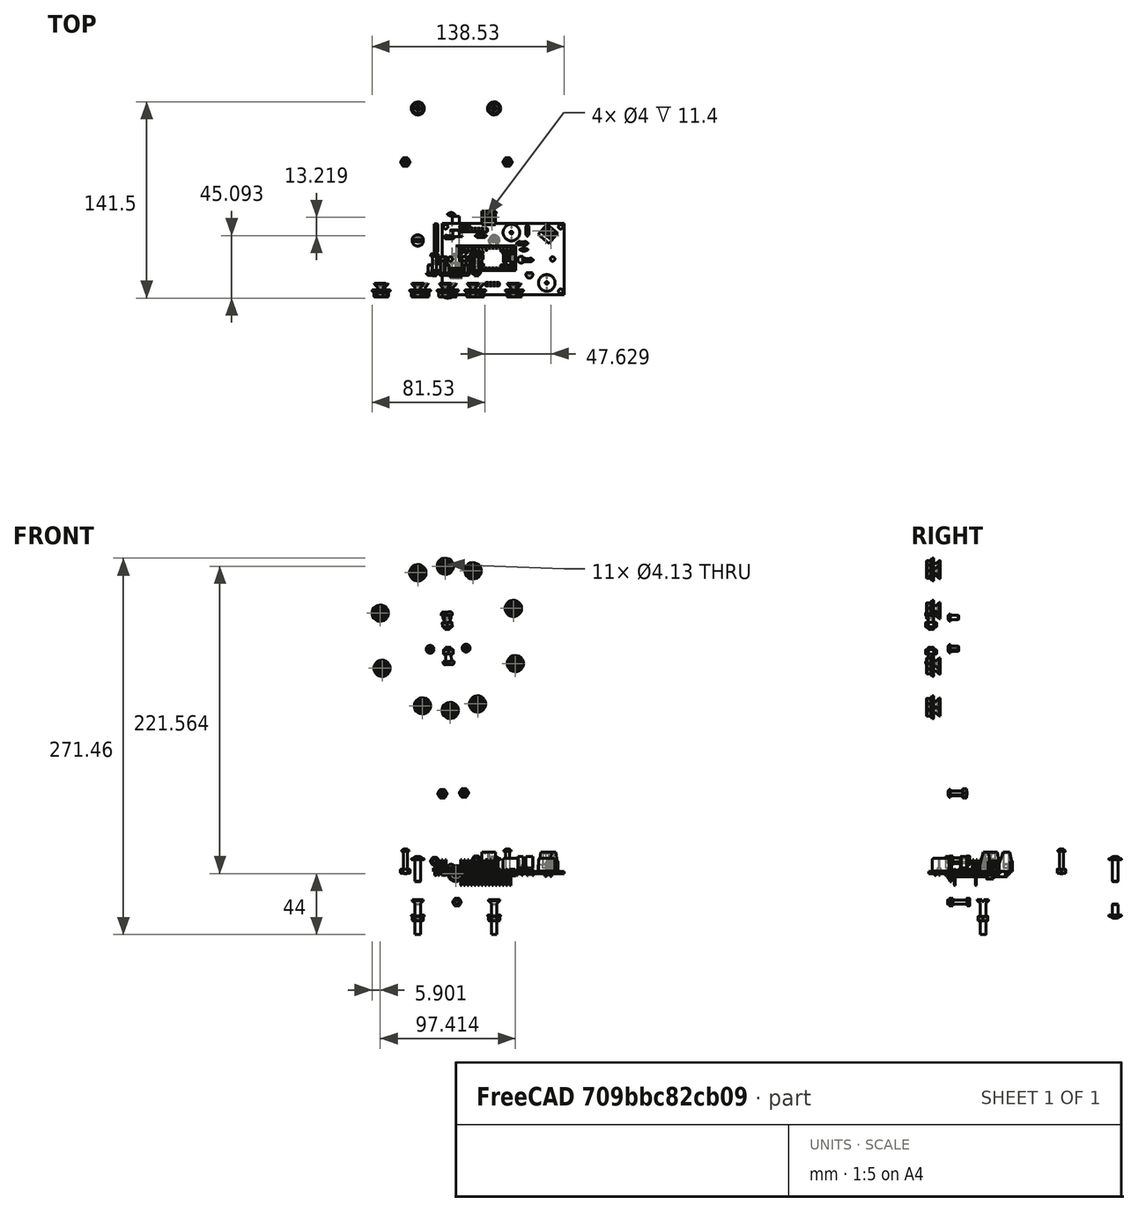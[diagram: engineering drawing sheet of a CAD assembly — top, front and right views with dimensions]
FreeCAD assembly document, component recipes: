
FREECAD ASSEMBLY — COMPONENT RECIPES ("assembly_Pendulum")

This assembly document has 17 components, labeled P0..P16 below (a component is one placed body or linked part). 14 of them carry a construction recipe — the FreeCAD feature program that regenerates the part from scratch, quoted from this document or its linked companion documents; the rest are supplied as boundary geometry only. No exploded tour is included for this assembly.
COMPONENT P0 — recipe-attached ("Body_Support", modeled in this document).
Construction recipe (the document's own serialized feature program — sketch geometry with constraints, then the solid features built on it; lengths are millimeters unless a unit is written):

FEATURE [Sketcher::SketchObject] Sketch
  ArcFitTolerance = 1e-06
  AttachmentSupport = -> [XZ_Plane001]
  ExternalTypes = [0]
  FullyConstrained = true
  MakeInternals = false
  MapMode = 5
  Placement = pos=(0,0,0) rot=(1,0,0;1.5708rad)
  _ExternalGeoVersion = 0
  sketch-geometry (13):
    g0: LineSegment StartX=5.6759 StartY=30.0968 StartZ=0 EndX=23.0689 EndY=6 EndZ=0
    g1: LineSegment StartX=23.0689 StartY=6 StartZ=0 EndX=34 EndY=6 EndZ=0
    g2: LineSegment StartX=34 StartY=6 StartZ=0 EndX=34 EndY=0 EndZ=0
    g3: LineSegment StartX=34 StartY=0 StartZ=0 EndX=20 EndY=0 EndZ=0
    g4: LineSegment StartX=20 StartY=0 StartZ=0 EndX=4.86567 EndY=20.9676 EndZ=0
    g5: LineSegment StartX=-4.86567 StartY=20.9676 StartZ=0 EndX=-20 EndY=0 EndZ=0
    g6: LineSegment StartX=-20 StartY=0 StartZ=0 EndX=-34 EndY=0 EndZ=0
    g7: LineSegment StartX=-34 StartY=0 StartZ=0 EndX=-34 EndY=6 EndZ=0
    g8: LineSegment StartX=-34 StartY=6 StartZ=0 EndX=-23.0689 EndY=6 EndZ=0
    g9: LineSegment StartX=-23.0689 StartY=6 StartZ=0 EndX=-5.6759 EndY=30.0968 EndZ=0
    g10: Circle CenterX=-1e-16 CenterY=26 CenterZ=0 NormalX=0 NormalY=0 NormalZ=1 AngleXU=0 Radius=2.8
    g11: ArcOfCircle CenterX=-1e-16 CenterY=26 CenterZ=0 NormalX=0 NormalY=0 NormalZ=1 AngleXU=0 Radius=7 StartAngle=0.625205 EndAngle=2.51639
    g12: ArcOfCircle CenterX=-1e-16 CenterY=26 CenterZ=0 NormalX=0 NormalY=0 NormalZ=1 AngleXU=0 Radius=7 StartAngle=3.94384 EndAngle=5.48094
  constraints (36):
    c: Coincident(g0,g1)
    c: Horizontal(g1)
    c: Coincident(g1,g2)
    c: PointOnObject(g2,g-1)
    c: Coincident(g2,g3)
    c: PointOnObject(g3,g-1)
    c: Coincident(g3,g4)
    c: Coincident(g5,g6)
    c: PointOnObject(g6,g-1)
    c: Coincident(g6,g7)
    c: Vertical(g7)
    c: Coincident(g7,g8)
    c: Horizontal(g8)
    c: Coincident(g8,g9)
    c: Symmetric(g9,g0,g-2)
    c: Parallel(g9,g5)
    c: Parallel(g0,g4)
    c: Vertical(g2)
    c: Equal(g7,g2)
    c: DistanceY(g7,g7) = 6
    c: Equal(g8,g1)
    c: DistanceX(g6,g6) = 14
    c: DistanceX(g5,g3) = 40
    c: Diameter(g10) = 5.6
    c: Coincident(g11,g10)
    c: Coincident(g11,g0)
    c: Equal(g11,g12)
    c: Coincident(g11,g12)
    c: Coincident(g4,g12)
    c: Coincident(g5,g12)
    c: DistanceY(g-1,g10) = 26
    c: Distance(g5,g9) = 6
    c: Distance(g4,g0) = 6
    c: Tangent(g9,g11) = 1.5708
    c: Diameter(g11) = 14
    c: Symmetric(g5,g3,g-2)
FEATURE [PartDesign::Pad] Pad  label="Pad_Main"
  Direction = (0,-1,2e-16)
  Length = 10
  Length2 = 10
  Placement = pos=(0,0,0) rot=(1,0,0;1.5708rad)
  Profile = -> Sketch
  ReferenceAxis = -> Sketch [N_Axis]
  Refine = true
  SideType = 0
  Suppressed = false
  Type = 0
  Type2 = 0
FEATURE [Sketcher::SketchObject] Sketch001
  ArcFitTolerance = 1e-06
  AttachmentSupport = -> [Pad]
  ExternalGeometry = -> [Pad]
  ExternalTypes = [0]
  FullyConstrained = true
  MakeInternals = false
  MapMode = 5
  Placement = pos=(0,-10,0) rot=(1,0,0;1.5708rad)
  _ExternalGeoVersion = 0
  sketch-geometry (2):
    g0: Circle CenterX=0 CenterY=26 CenterZ=0 NormalX=0 NormalY=0 NormalZ=1 AngleXU=0 Radius=3.8
    g1: Circle CenterX=0 CenterY=26 CenterZ=0 NormalX=0 NormalY=0 NormalZ=1 AngleXU=0 Radius=2.8
  constraints (4):
    c: Coincident(g0,g-3)
    c: Coincident(g1,g0)
    c: Diameter(g1) = 5.6
    c: Diameter(g0) = 7.6
FEATURE [PartDesign::Pad] Pad001  label="Pad_Shaft"
  BaseFeature = -> Pad
  Direction = (0,-1,2e-16)
  Length = 16.6
  Length2 = 10
  Placement = pos=(0,0,0) rot=(1,0,0;1.5708rad)
  Profile = -> Sketch001
  ReferenceAxis = -> Sketch001 [N_Axis]
  Refine = true
  SideType = 0
  Suppressed = false
  Type = 0
  Type2 = 0
FEATURE [Sketcher::SketchObject] Sketch002
  ArcFitTolerance = 1e-06
  AttachmentSupport = -> [Pad001]
  ExternalGeometry = -> [Pad001]
  ExternalTypes = [0]
  FullyConstrained = true
  MakeInternals = false
  MapMode = 5
  Placement = pos=(0,-10,0) rot=(1,0,0;1.5708rad)
  _ExternalGeoVersion = 0
  sketch-geometry (2):
    g0: Circle CenterX=0 CenterY=26 CenterZ=0 NormalX=0 NormalY=0 NormalZ=1 AngleXU=0 Radius=3.8
    g1: Circle CenterX=0 CenterY=26 CenterZ=0 NormalX=0 NormalY=0 NormalZ=1 AngleXU=0 Radius=6.5
  constraints (4):
    c: Coincident(g0,g-3)
    c: Equal(g0,g-3)
    c: Coincident(g1,g0)
    c: Diameter(g1) = 13
FEATURE [PartDesign::Pad] Pad002  label="Pad_Thrust"
  BaseFeature = -> Pad001
  Direction = (0,-1,2e-16)
  Length = 10
  Length2 = 10
  Placement = pos=(0,0,0) rot=(1,0,0;1.5708rad)
  Profile = -> Sketch002
  ReferenceAxis = -> Sketch002 [N_Axis]
  Refine = true
  SideType = 0
  Suppressed = false
  Type = 0
  Type2 = 0
FEATURE [Sketcher::SketchObject] Sketch003
  ArcFitTolerance = 1e-06
  AttachmentSupport = -> [Pad002]
  ExternalTypes = [0]
  FullyConstrained = true
  MakeInternals = false
  MapMode = 5
  Placement = pos=(0,2.9e-15,0) rot=(-1,0,0;1.5708rad)
  _ExternalGeoVersion = 0
  sketch-geometry (7):
    g0: LineSegment StartX=-4.8 StartY=-26 StartZ=0 EndX=-2.4 EndY=-30.1569 EndZ=0
    g1: LineSegment StartX=-2.4 StartY=-30.1569 StartZ=0 EndX=2.4 EndY=-30.1569 EndZ=0
    g2: LineSegment StartX=2.4 StartY=-30.1569 StartZ=0 EndX=4.8 EndY=-26 EndZ=0
    g3: LineSegment StartX=4.8 StartY=-26 StartZ=0 EndX=2.4 EndY=-21.8431 EndZ=0
    g4: LineSegment StartX=2.4 StartY=-21.8431 StartZ=0 EndX=-2.4 EndY=-21.8431 EndZ=0
    g5: LineSegment StartX=-2.4 StartY=-21.8431 StartZ=0 EndX=-4.8 EndY=-26 EndZ=0
    g6: Circle [constr] CenterX=0 CenterY=-26 CenterZ=0 NormalX=0 NormalY=0 NormalZ=1 AngleXU=0 Radius=4.8
  constraints (16):
    c: Coincident(g0,g1)
    c: Coincident(g1,g2)
    c: Coincident(g2,g3)
    c: Coincident(g3,g4)
    c: Coincident(g4,g5)
    c: Coincident(g5,g0)
    c: Equal(g0, g1-g5) x5
    c: PointOnObject(g0,g6)
    c: PointOnObject(g1,g6)
    c: PointOnObject(g2,g6)
    c: PointOnObject(g3,g6)
    c: PointOnObject(g4,g6)
    c: PointOnObject(g5,g6)
    c: Coincident(g6,g-3)
    c: Horizontal(g4)
    c: Diameter(g6) = 9.6
FEATURE [PartDesign::Pocket] Pocket
  BaseFeature = -> Pad002
  Direction = (0,-1,-2e-16)
  Length = 3
  Length2 = 5
  Placement = pos=(0,0,0) rot=(1,0,0;1.5708rad)
  Profile = -> Sketch003
  ReferenceAxis = -> Sketch003 [N_Axis]
  Refine = true
  SideType = 0
  Suppressed = false
  Type = 0
  Type2 = 0
FEATURE [PartDesign::CoordinateSystem] Support
  AttacherType = Attacher::AttachEngine3D
  AttachmentOffset = pos=(0,0,0) rot=(-0.57735,0.57735,-0.57735;2.0944rad)
  AttachmentSupport = -> [Pocket]
  MapMode = 11
  Placement = pos=(0,-26.6,26) rot=(0,0,1;0rad)
FEATURE [Sketcher::SketchObject] Sketch050
  ArcFitTolerance = 1e-06
  AttachmentSupport = -> [XY_Plane001]
  ExternalTypes = [0]
  FullyConstrained = true
  MakeInternals = false
  MapMode = 5
  _ExternalGeoVersion = 0
  sketch-geometry (2):
    g0: Circle CenterX=-27.5 CenterY=-5 CenterZ=0 NormalX=0 NormalY=0 NormalZ=1 AngleXU=0 Radius=2.3
    g1: Circle CenterX=27.5 CenterY=-5 CenterZ=0 NormalX=0 NormalY=0 NormalZ=1 AngleXU=0 Radius=2.3
  constraints (5):
    c: Equal(g1,g0)
    c: Diameter(g1) = 4.6
    c: DistanceX(g0,g1) = 55
    c: DistanceY(g1,g-1) = 5
    c: Symmetric(g1,g0,g-2)
FEATURE [PartDesign::Pocket] Pocket015
  BaseFeature = -> Pocket
  Direction = (0,0,-1)
  Length = 5
  Length2 = 5
  Placement = pos=(0,0,0) rot=(1,0,0;1.5708rad)
  Profile = -> Sketch050
  ReferenceAxis = -> Sketch050 [N_Axis]
  Refine = true
  Reversed = true
  SideType = 0
  Suppressed = false
  Type = 1
  Type2 = 0
FEATURE [PartDesign::Chamfer] Chamfer003
  Angle = 45
  Base = -> Pocket015 [Edge47,Edge40]
  BaseFeature = -> Pocket015
  ChamferType = 0
  FlipDirection = false
  Placement = pos=(0,0,0) rot=(1,0,0;1.5708rad)
  Refine = true
  Size = 1.5
  Size2 = 1
  SupportTransform = false
  Suppressed = false
  UseAllEdges = false
FEATURE [PartDesign::CoordinateSystem] Support_Foot
  AttacherType = Attacher::AttachEngine3D
  AttachmentOffset = pos=(0,0,0) rot=(0.866025,-0.5,0;3.14159rad)
  AttachmentSupport = -> [Pocket015]
  MapMode = 11
  Placement = pos=(-27.5,-5,6) rot=(0,0,1;5.75959rad)
FEATURE [PartDesign::Fillet] Fillet010
  Base = -> Pocket015 [Edge31,Edge16,Edge13,Edge28]
  BaseFeature = -> Pocket015
  Placement = pos=(0,0,0) rot=(1,0,0;1.5708rad)
  Radius = 4.99
  Refine = true
  SupportTransform = false
  Suppressed = false
  UseAllEdges = false
FEATURE [PartDesign::Body] Body  label="Body_Support"
  AllowCompound = false
  Description = Pendulum
  Group = -> [Sketch,Pad,Sketch001,Pad001,Sketch002,Pad002,Sketch003,Pocket,Support,Sketch050,Pocket015,Chamfer003,Support_Foot,Fillet010]
  Origin = -> Origin001
  Tip = -> Fillet010
COMPONENT P1 — recipe-attached ("Body_Bearing", modeled in this document).
Construction recipe (the document's own serialized feature program — sketch geometry with constraints, then the solid features built on it; lengths are millimeters unless a unit is written):

FEATURE [Sketcher::SketchObject] Sketch005  label="Sketch_section"
  ArcFitTolerance = 0
  AttachmentSupport = -> [XZ_Plane003]
  ExternalTypes = [0]
  FullyConstrained = true
  MakeInternals = false
  MapMode = 5
  Placement = pos=(0,0,0) rot=(1,0,0;1.5708rad)
  _ExternalGeoVersion = 0
  sketch-geometry (12):
    g0: LineSegment StartX=4 StartY=-3.5 StartZ=0 EndX=6.5 EndY=-3.5 EndZ=0
    g1: LineSegment StartX=11 StartY=-3.5 StartZ=0 EndX=11 EndY=3.5 EndZ=0
    g2: LineSegment StartX=11 StartY=3.5 StartZ=0 EndX=9.25 EndY=3.5 EndZ=0
    g3: LineSegment StartX=4 StartY=3.5 StartZ=0 EndX=4 EndY=-3.5 EndZ=0
    g4: LineSegment StartX=6.5 StartY=3.5 StartZ=0 EndX=6.75 EndY=3.25 EndZ=0
    g5: LineSegment StartX=6.75 StartY=3.25 StartZ=0 EndX=9 EndY=3.25 EndZ=0
    g6: LineSegment StartX=9 StartY=3.25 StartZ=0 EndX=9.25 EndY=3.5 EndZ=0
    g7: LineSegment StartX=6.5 StartY=-3.5 StartZ=0 EndX=6.75 EndY=-3.25 EndZ=0
    g8: LineSegment StartX=6.75 StartY=-3.25 StartZ=0 EndX=9 EndY=-3.25 EndZ=0
    g9: LineSegment StartX=9 StartY=-3.25 StartZ=0 EndX=9.25 EndY=-3.5 EndZ=0
    g10: LineSegment StartX=6.5 StartY=3.5 StartZ=0 EndX=4 EndY=3.5 EndZ=0
    g11: LineSegment StartX=9.25 StartY=-3.5 StartZ=0 EndX=11 EndY=-3.5 EndZ=0
  constraints (33):
    c: Coincident(g11,g1)
    c: Coincident(g1,g2)
    c: Coincident(g10,g3)
    c: Coincident(g3,g0)
    c: Horizontal(g0)
    c: Horizontal(g2)
    c: Vertical(g1)
    c: DistanceY(g1) = 7
    c: DistanceX(g0) = 4
    c: DistanceX(g11) = 11
    c: Coincident(g4,g5)
    c: Horizontal(g5)
    c: Coincident(g5,g6)
    c: Coincident(g7,g8)
    c: Horizontal(g8)
    c: Coincident(g8,g9)
    c: Coincident(g2,g6)
    c: Coincident(g10,g4)
    c: Tangent(g2,g10)
    c: Coincident(g0,g7)
    c: Coincident(g11,g9)
    c: Tangent(g0,g11)
    c: Equal(g4,g6)
    c: Equal(g6,g7)
    c: Angle(g10,g4) = 2.35619
    c: DistanceX(g2) = -1.75
    c: DistanceX(g10) = -2.5
    c: Equal(g0,g10)
    c: Equal(g11,g2)
    c: Equal(g9,g7)
    c: Parallel(g9,g4)
    c: DistanceY(g5,g1) = 0.25
    c: Symmetric(g0,g3,g-1)
FEATURE [PartDesign::Revolution] Revolution
  Angle = 360
  Angle2 = 60
  Axis = (0,2e-16,1)
  Base = (0,0,0)
  FuseOrder = 1
  Placement = pos=(0,0,0) rot=(1,0,0;1.5708rad)
  Profile = -> Sketch005
  ReferenceAxis = -> Sketch005 [V_Axis]
  Refine = true
  Suppressed = false
  Type = 0
FEATURE [PartDesign::Chamfer] Chamfer
  Angle = 45
  Base = -> Revolution [Edge12,Edge11]
  BaseFeature = -> Revolution
  ChamferType = 0
  FlipDirection = false
  Placement = pos=(0,0,0) rot=(1,0,0;1.5708rad)
  Refine = true
  Size = 0.25
  Size2 = 1
  SupportTransform = false
  Suppressed = false
  UseAllEdges = false
FEATURE [PartDesign::CoordinateSystem] Bearing_Axis
  AttacherType = Attacher::AttachEngine3D
  AttachmentSupport = -> [Chamfer]
  MapMode = 45
  Placement = pos=(1.89e-14,1.7e-15,3.5) rot=(0,0,1;0rad)
FEATURE [PartDesign::Body] Body002  label="Body_Bearing"
  AllowCompound = false
  Group = -> [Sketch005,Revolution,Chamfer,Bearing_Axis]
  Origin = -> Origin003
  Tip = -> Chamfer
COMPONENT P2 — recipe-attached ("Body_Arm", modeled in this document).
Construction recipe (the document's own serialized feature program — sketch geometry with constraints, then the solid features built on it; lengths are millimeters unless a unit is written):

FEATURE [Sketcher::SketchObject] Sketch006
  ArcFitTolerance = 1e-06
  AttachmentSupport = -> [XY_Plane004]
  ExternalTypes = [0]
  FullyConstrained = true
  MakeInternals = false
  MapMode = 5
  _ExternalGeoVersion = 0
  sketch-geometry (1):
    g0: Circle CenterX=0 CenterY=84.85 CenterZ=0 NormalX=0 NormalY=0 NormalZ=1 AngleXU=0 Radius=23
  constraints (3):
    c: PointOnObject(g0,g-2)
    c: DistanceY(g-1,g0) = 84.85
    c: Diameter(g0) = 46
FEATURE [Sketcher::SketchObject] Sketch007
  ArcFitTolerance = 1e-06
  AttachmentSupport = -> [XY_Plane004]
  ExternalTypes = [0]
  FullyConstrained = true
  MakeInternals = false
  MapMode = 5
  _ExternalGeoVersion = 0
  sketch-geometry (33):
    g0: LineSegment StartX=-18 StartY=67.5 StartZ=0 EndX=-18 EndY=-67.5 EndZ=0
    g1: LineSegment StartX=18 StartY=-67.5 StartZ=0 EndX=18 EndY=67.5 EndZ=0
    g2: ArcOfCircle CenterX=0 CenterY=84.8494 CenterZ=0 NormalX=0 NormalY=0 NormalZ=1 AngleXU=0 Radius=25 StartAngle=5.51619 EndAngle=10.1918
    g3: Circle CenterX=0 CenterY=84.8494 CenterZ=0 NormalX=0 NormalY=0 NormalZ=1 AngleXU=0 Radius=11.5
    g4: Circle CenterX=0 CenterY=99.8494 CenterZ=0 NormalX=0 NormalY=0 NormalZ=1 AngleXU=0 Radius=1.8
    g5: Circle CenterX=9.64181 CenterY=96.34 CenterZ=0 NormalX=0 NormalY=0 NormalZ=1 AngleXU=0 Radius=1.8
    g6: Circle CenterX=14.7721 CenterY=87.4541 CenterZ=0 NormalX=0 NormalY=0 NormalZ=1 AngleXU=0 Radius=1.8
    g7: Circle CenterX=12.9904 CenterY=77.3494 CenterZ=0 NormalX=0 NormalY=0 NormalZ=1 AngleXU=0 Radius=1.8
    g8: Circle CenterX=5.1303 CenterY=70.754 CenterZ=0 NormalX=0 NormalY=0 NormalZ=1 AngleXU=0 Radius=1.8
    g9: Circle CenterX=-5.1303 CenterY=70.754 CenterZ=0 NormalX=0 NormalY=0 NormalZ=1 AngleXU=0 Radius=1.8
    g10: Circle CenterX=-12.9904 CenterY=77.3494 CenterZ=0 NormalX=0 NormalY=0 NormalZ=1 AngleXU=0 Radius=1.8
    g11: Circle CenterX=-14.7721 CenterY=87.4541 CenterZ=0 NormalX=0 NormalY=0 NormalZ=1 AngleXU=0 Radius=1.8
    g12: Circle CenterX=-9.64181 CenterY=96.34 CenterZ=0 NormalX=0 NormalY=0 NormalZ=1 AngleXU=0 Radius=1.8
    g13: LineSegment [constr] StartX=-9.64181 StartY=96.34 StartZ=0 EndX=0 EndY=84.8494 EndZ=0
    g14: LineSegment [constr] StartX=-14.7721 StartY=87.4541 StartZ=0 EndX=0 EndY=84.8494 EndZ=0
    g15: LineSegment [constr] StartX=-12.9904 StartY=77.3494 StartZ=0 EndX=0 EndY=84.8494 EndZ=0
    g16: LineSegment [constr] StartX=-5.1303 StartY=70.754 StartZ=0 EndX=0 EndY=84.8494 EndZ=0
    g17: LineSegment [constr] StartX=5.1303 StartY=70.754 StartZ=0 EndX=0 EndY=84.8494 EndZ=0
    g18: LineSegment [constr] StartX=12.9904 StartY=77.3494 StartZ=0 EndX=0 EndY=84.8494 EndZ=0
    g19: LineSegment [constr] StartX=14.7721 StartY=87.4541 StartZ=0 EndX=0 EndY=84.8494 EndZ=0
    g20: LineSegment [constr] StartX=9.64181 StartY=96.34 StartZ=0 EndX=0 EndY=84.8494 EndZ=0
    g21: Circle CenterX=-7.78 CenterY=-27 CenterZ=0 NormalX=0 NormalY=0 NormalZ=1 AngleXU=0 Radius=1.8
    g22: Circle CenterX=7.78 CenterY=-27 CenterZ=0 NormalX=0 NormalY=0 NormalZ=1 AngleXU=0 Radius=1.8
    g23: ArcOfCircle CenterX=0 CenterY=-84.8494 CenterZ=0 NormalX=0 NormalY=0 NormalZ=1 AngleXU=0 Radius=25 StartAngle=2.3746 EndAngle=7.05018
    g24: Circle CenterX=0 CenterY=-84.8494 CenterZ=0 NormalX=0 NormalY=0 NormalZ=1 AngleXU=0 Radius=11.25
    g25: LineSegment StartX=-12.5 StartY=63.1987 StartZ=0 EndX=-12.5 EndY=-16.8013 EndZ=0
    g26: LineSegment StartX=-12.5 StartY=-16.8013 StartZ=0 EndX=12.5 EndY=-16.8013 EndZ=0
    g27: LineSegment StartX=12.5 StartY=-16.8013 StartZ=0 EndX=12.5 EndY=63.1987 EndZ=0
    g28: LineSegment StartX=-12.5 StartY=-33.5 StartZ=0 EndX=-12.5 EndY=-67.5 EndZ=0
    g29: LineSegment StartX=-12.5 StartY=-67.5 StartZ=0 EndX=12.5 EndY=-67.5 EndZ=0
    g30: LineSegment StartX=12.5 StartY=-67.5 StartZ=0 EndX=12.5 EndY=-33.5 EndZ=0
    g31: LineSegment StartX=12.5 StartY=-33.5 StartZ=0 EndX=-12.5 EndY=-33.5 EndZ=0
    g32: ArcOfCircle CenterX=0 CenterY=84.8494 CenterZ=0 NormalX=0 NormalY=0 NormalZ=1 AngleXU=0 Radius=25 StartAngle=4.18879 EndAngle=5.23599
  constraints (88):
    c: Vertical(g0)
    c: Vertical(g1)
    c: Symmetric(g0,g1,g-1)
    c: DistanceX(g0,g1) = 36
    c: DistanceY(g1,g1) = 135
    c: PointOnObject(g2,g-2)
    c: Diameter(g2) = 50
    c: Coincident(g2,g0)
    c: Coincident(g2,g1)
    c: Coincident(g3,g2)
    c: Diameter(g3) = 23
    c: PointOnObject(g4,g-2)
    c: Coincident(g13,g12)
    c: Coincident(g13,g2)
    c: Coincident(g14,g11)
    c: Coincident(g14,g2)
    c: Coincident(g15,g10)
    c: Coincident(g15,g2)
    c: Coincident(g16,g9)
    c: Coincident(g16,g2)
    c: Coincident(g17,g8)
    c: Coincident(g17,g2)
    c: Coincident(g18,g7)
    c: Coincident(g18,g2)
    c: Coincident(g19,g6)
    c: Coincident(g19,g2)
    c: Coincident(g20,g5)
    c: Coincident(g20,g2)
    c: Equal(g4,g5)
    c: Equal(g5,g6)
    c: Equal(g6,g7)
    c: Equal(g7,g8)
    c: Equal(g8,g9)
    c: Equal(g9,g10)
    c: Equal(g10,g11)
    c: Equal(g11,g12)
    c: Equal(g13,g14)
    c: Equal(g14,g15)
    c: Equal(g15,g16)
    c: Equal(g16,g17)
    c: Equal(g17,g18)
    c: Equal(g18,g19)
    c: Equal(g19,g20)
    c: DistanceY(g2,g4) = 15
    c: Distance(g13) = 15
    c: Diameter(g4) = 3.6
    c: Angle(g-2,g20) = 2.44346
    c: Angle(g19,g20) = 0.698132
    c: Angle(g18,g19) = 0.698132
    c: Angle(g17,g18) = 0.698132
    c: Angle(g16,g17) = 0.698132
    c: Angle(g15,g16) = 0.698132
    c: Angle(g14,g15) = 0.698132
    c: Angle(g13,g14) = 0.698132
    c: Equal(g22,g21)
    c: Diameter(g21) = 3.6
    c: DistanceX(g21,g22) = 15.56
    c: Symmetric(g21,g22,g-2)
    c: DistanceY(g22,g-1) = 27
    c: PointOnObject(g23,g-2)
    c: Diameter(g23) = 50
    c: Coincident(g23,g1)
    c: Coincident(g23,g0)
    c: Coincident(g24,g23)
    c: Diameter(g24) = 22.5
    c: Vertical(g25)
    c: Vertical(g27)
    c: Horizontal(g26)
    c: Coincident(g28,g29)
    c: Coincident(g29,g30)
    c: Coincident(g30,g31)
    c: Coincident(g31,g28)
    c: Vertical(g28)
    c: Vertical(g30)
    c: Horizontal(g29)
    c: Symmetric(g27,g25,g-2)
    c: DistanceY(g25,g25) = 80
    c: DistanceX(g25,g27) = 25
    c: PointOnObject(g1,g29)
    c: Symmetric(g28,g30,g-2)
    c: DistanceX(g31,g31) = 25
    c: DistanceY(g28,g28) = 34
    c: Diameter(g32) = 50
    c: Coincident(g32,g25)
    c: Coincident(g32,g27)
    c: Coincident(g32,g2)
    c: Coincident(g26,g25)
    c: Coincident(g27,g26)
FEATURE [PartDesign::Pad] Pad004  label="Pad_Arm"
  Direction = (0,0,1)
  Length = 8
  Length2 = 10
  Profile = -> Sketch007
  ReferenceAxis = -> Sketch007 [N_Axis]
  Refine = true
  SideType = 0
  Suppressed = false
  Type = 0
  Type2 = 0
FEATURE [PartDesign::Pocket] Pocket001  label="Pocket_Motor"
  BaseFeature = -> Pad004
  Direction = (0,0,-1)
  Length = 3
  Length2 = 5
  Profile = -> Sketch006
  ReferenceAxis = -> Sketch006 [N_Axis]
  Refine = true
  Reversed = true
  SideType = 0
  Suppressed = false
  Type = 0
  Type2 = 0
FEATURE [PartDesign::CoordinateSystem] Arm_Axis_Top
  AttacherType = Attacher::AttachEngine3D
  AttachmentOffset = pos=(0,0,0) rot=(0,0,-1;1.5708rad)
  AttachmentSupport = -> [Pocket001]
  MapMode = 11
  Placement = pos=(2e-16,99.8494,8) rot=(0,0,1;0rad)
FEATURE [PartDesign::CoordinateSystem] Arm_MPU6050_Right
  AttacherType = Attacher::AttachEngine3D
  AttachmentOffset = pos=(0,0,0) rot=(-1,0,0;1.5708rad)
  AttachmentSupport = -> [Pocket001]
  MapMode = 11
  Placement = pos=(-7.78,-27,0) rot=(-0.57735,-0.57735,0.57735;2.0944rad)
FEATURE [PartDesign::Chamfer] Chamfer002
  Angle = 45
  Base = -> Pocket001 [Edge44,Edge45]
  BaseFeature = -> Pocket001
  ChamferType = 0
  FlipDirection = false
  Refine = true
  Size = 1.5
  Size2 = 1
  SupportTransform = false
  Suppressed = false
  UseAllEdges = false
FEATURE [Sketcher::SketchObject] Sketch027
  ArcFitTolerance = 1e-06
  AttachmentSupport = -> [Chamfer002]
  ExternalGeometry = -> [Chamfer002]
  ExternalTypes = [0]
  FullyConstrained = true
  MakeInternals = false
  MapMode = 5
  Placement = pos=(0,0,8) rot=(0,0,1;0rad)
  _ExternalGeoVersion = 0
  sketch-geometry (3):
    g0: ArcOfCircle CenterX=0 CenterY=-84.8494 CenterZ=0 NormalX=0 NormalY=0 NormalZ=1 AngleXU=0 Radius=25 StartAngle=2.3746 EndAngle=7.05018
    g1: LineSegment StartX=-18 StartY=-67.5 StartZ=0 EndX=18 EndY=-67.5 EndZ=0
    g2: Circle CenterX=0 CenterY=-84.8494 CenterZ=0 NormalX=0 NormalY=0 NormalZ=1 AngleXU=0 Radius=9
  constraints (7):
    c: Coincident(g0,g-3)
    c: Coincident(g1,g-3)
    c: Coincident(g0,g1)
    c: Coincident(g0,g1)
    c: Horizontal(g1)
    c: Coincident(g2,g0)
    c: Diameter(g2) = 18
FEATURE [PartDesign::Pad] Pad017  label="Pad_LockBearing"
  BaseFeature = -> Chamfer002
  Direction = (0,0,1)
  Length = 2
  Length2 = 10
  Profile = -> Sketch027
  ReferenceAxis = -> Sketch027 [N_Axis]
  Refine = true
  Reversed = true
  SideType = 0
  Suppressed = false
  Type = 0
  Type2 = 0
FEATURE [Sketcher::SketchObject] Sketch032
  ArcFitTolerance = 1e-06
  AttachmentSupport = -> [Pad017]
  ExternalGeometry = -> [Pad017]
  ExternalTypes = [0]
  FullyConstrained = true
  MakeInternals = false
  MapMode = 5
  Placement = pos=(0,0,8) rot=(0,0,1;0rad)
  _ExternalGeoVersion = 0
  sketch-geometry (3):
    g0: Circle CenterX=-15 CenterY=-75.5 CenterZ=0 NormalX=0 NormalY=0 NormalZ=1 AngleXU=0 Radius=1.8
    g1: Circle CenterX=15 CenterY=-75.5 CenterZ=0 NormalX=0 NormalY=0 NormalZ=1 AngleXU=0 Radius=1.8
    g2: Circle CenterX=0 CenterY=-105.5 CenterZ=0 NormalX=0 NormalY=0 NormalZ=1 AngleXU=0 Radius=1.8
  constraints (8):
    c: PointOnObject(g2,g-2)
    c: Equal(g2,g1)
    c: Equal(g1,g0)
    c: Diameter(g0) = 3.6
    c: DistanceY(g0,g-3) = 8
    c: DistanceY(g2,g0) = 30
    c: Symmetric(g0,g1,g-2)
    c: DistanceX(g0,g1) = 30
FEATURE [PartDesign::Pocket] Pocket009
  BaseFeature = -> Pad017
  Direction = (0,0,-1)
  Length = 5
  Length2 = 5
  Profile = -> Sketch032
  ReferenceAxis = -> Sketch032 [N_Axis]
  Refine = true
  SideType = 0
  Suppressed = false
  Type = 1
  Type2 = 0
FEATURE [Sketcher::SketchObject] Sketch033
  ArcFitTolerance = 1e-06
  AttachmentSupport = -> [Pocket009]
  ExternalGeometry = -> [Pocket009]
  ExternalTypes = [0]
  FullyConstrained = true
  MakeInternals = false
  MapMode = 5
  Placement = pos=(0,0,8) rot=(0,0,1;0rad)
  _ExternalGeoVersion = 0
  sketch-geometry (21):
    g0: LineSegment StartX=-13.35 StartY=-78.3579 StartZ=0 EndX=-11.7 EndY=-75.5 EndZ=0
    g1: LineSegment StartX=-11.7 StartY=-75.5 StartZ=0 EndX=-13.35 EndY=-72.6421 EndZ=0
    g2: LineSegment StartX=-13.35 StartY=-72.6421 StartZ=0 EndX=-16.65 EndY=-72.6421 EndZ=0
    g3: LineSegment StartX=-16.65 StartY=-72.6421 StartZ=0 EndX=-18.3 EndY=-75.5 EndZ=0
    g4: LineSegment StartX=-18.3 StartY=-75.5 StartZ=0 EndX=-16.65 EndY=-78.3579 EndZ=0
    g5: LineSegment StartX=-16.65 StartY=-78.3579 StartZ=0 EndX=-13.35 EndY=-78.3579 EndZ=0
    g6: Circle [constr] CenterX=-15 CenterY=-75.5 CenterZ=0 NormalX=0 NormalY=0 NormalZ=1 AngleXU=0 Radius=3.3
    g7: LineSegment StartX=16.65 StartY=-72.6421 StartZ=0 EndX=13.35 EndY=-72.6421 EndZ=0
    g8: LineSegment StartX=13.35 StartY=-72.6421 StartZ=0 EndX=11.7 EndY=-75.5 EndZ=0
    g9: LineSegment StartX=11.7 StartY=-75.5 StartZ=0 EndX=13.35 EndY=-78.3579 EndZ=0
    g10: LineSegment StartX=13.35 StartY=-78.3579 StartZ=0 EndX=16.65 EndY=-78.3579 EndZ=0
    g11: LineSegment StartX=16.65 StartY=-78.3579 StartZ=0 EndX=18.3 EndY=-75.5 EndZ=0
    g12: LineSegment StartX=18.3 StartY=-75.5 StartZ=0 EndX=16.65 EndY=-72.6421 EndZ=0
    g13: Circle [constr] CenterX=15 CenterY=-75.5 CenterZ=0 NormalX=0 NormalY=0 NormalZ=1 AngleXU=0 Radius=3.3
    g14: LineSegment StartX=1.65 StartY=-102.642 StartZ=0 EndX=-1.65 EndY=-102.642 EndZ=0
    g15: LineSegment StartX=-1.65 StartY=-102.642 StartZ=0 EndX=-3.3 EndY=-105.5 EndZ=0
    g16: LineSegment StartX=-3.3 StartY=-105.5 StartZ=0 EndX=-1.65 EndY=-108.358 EndZ=0
    g17: LineSegment StartX=-1.65 StartY=-108.358 StartZ=0 EndX=1.65 EndY=-108.358 EndZ=0
    g18: LineSegment StartX=1.65 StartY=-108.358 StartZ=0 EndX=3.3 EndY=-105.5 EndZ=0
    g19: LineSegment StartX=3.3 StartY=-105.5 StartZ=0 EndX=1.65 EndY=-102.642 EndZ=0
    g20: Circle [constr] CenterX=0 CenterY=-105.5 CenterZ=0 NormalX=0 NormalY=0 NormalZ=1 AngleXU=0 Radius=3.3
  constraints (48):
    c: Coincident(g0,g1)
    c: Coincident(g1,g2)
    c: Coincident(g2,g3)
    c: Coincident(g3,g4)
    c: Coincident(g4,g5)
    c: Coincident(g5,g0)
    c: Equal(g0, g1-g5) x5
    c: PointOnObject(g0,g6)
    c: PointOnObject(g1,g6)
    c: PointOnObject(g2,g6)
    c: PointOnObject(g3,g6)
    c: PointOnObject(g4,g6)
    c: PointOnObject(g5,g6)
    c: Coincident(g6,g-3)
    c: Coincident(g7,g8)
    c: Coincident(g8,g9)
    c: Coincident(g9,g10)
    c: Coincident(g10,g11)
    c: Coincident(g11,g12)
    c: Coincident(g12,g7)
    c: Equal(g7, g8-g12) x5
    c: PointOnObject(g7,g13)
    c: PointOnObject(g8,g13)
    c: PointOnObject(g9,g13)
    c: PointOnObject(g10,g13)
    c: PointOnObject(g11,g13)
    c: PointOnObject(g12,g13)
    c: Coincident(g13,g-4)
    c: Coincident(g14,g15)
    c: Coincident(g15,g16)
    c: Coincident(g16,g17)
    c: Coincident(g17,g18)
    c: Coincident(g18,g19)
    c: Coincident(g19,g14)
    c: Equal(g14, g15-g19) x5
    c: PointOnObject(g14,g20)
    c: PointOnObject(g15,g20)
    c: PointOnObject(g16,g20)
    c: PointOnObject(g17,g20)
    c: PointOnObject(g18,g20)
    c: PointOnObject(g19,g20)
    c: Coincident(g20,g-5)
    c: Equal(g13,g6)
    c: Equal(g6,g20)
    c: Diameter(g13) = 6.6
    c: Horizontal(g2)
    c: Horizontal(g7)
    c: Horizontal(g14)
FEATURE [PartDesign::Pocket] Pocket010
  BaseFeature = -> Pocket009
  Direction = (0,0,-1)
  Length = 3
  Length2 = 5
  Profile = -> Sketch033
  ReferenceAxis = -> Sketch033 [N_Axis]
  Refine = true
  SideType = 0
  Suppressed = false
  Type = 0
  Type2 = 0
FEATURE [PartDesign::CoordinateSystem] Arm_Axis_Bottom
  AttacherType = Attacher::AttachEngine3D
  AttachmentSupport = -> [Pocket010]
  MapMode = 45
  Placement = pos=(4.26e-14,-84.8494,8) rot=(0,0,1;0rad)
FEATURE [PartDesign::Body] Body003  label="Body_Arm"
  AllowCompound = false
  Group = -> [Sketch007,Pad004,Sketch006,Pocket001,Arm_Axis_Top,Arm_MPU6050_Right,Chamfer002,Sketch027,Pad017,Sketch032,Pocket009,Sketch033,Pocket010,Arm_Axis_Bottom]
  Origin = -> Origin004
  Tip = -> Pocket010
COMPONENT P3 — recipe-attached ("Body_ReactionWheel", modeled in this document).
Construction recipe (the document's own serialized feature program — sketch geometry with constraints, then the solid features built on it; lengths are millimeters unless a unit is written):

FEATURE [Sketcher::SketchObject] Sketch008
  ArcFitTolerance = 1e-06
  AttachmentSupport = -> [XZ_Plane005]
  ExternalTypes = [0]
  FullyConstrained = true
  MakeInternals = false
  MapMode = 5
  Placement = pos=(0,0,0) rot=(1,0,0;1.5708rad)
  _ExternalGeoVersion = 0
  sketch-geometry (8):
    g0: LineSegment StartX=-3.7 StartY=11.6 StartZ=0 EndX=-3.7 EndY=8 EndZ=0
    g1: LineSegment StartX=-3.7 StartY=8 StartZ=0 EndX=3.7 EndY=8 EndZ=0
    g2: LineSegment StartX=3.7 StartY=8 StartZ=0 EndX=3.7 EndY=11.6 EndZ=0
    g3: LineSegment StartX=3.7 StartY=11.6 StartZ=0 EndX=-3.7 EndY=11.6 EndZ=0
    g4: LineSegment StartX=-3.7 StartY=-8 StartZ=0 EndX=-3.7 EndY=-11.6 EndZ=0
    g5: LineSegment StartX=-3.7 StartY=-11.6 StartZ=0 EndX=3.7 EndY=-11.6 EndZ=0
    g6: LineSegment StartX=3.7 StartY=-11.6 StartZ=0 EndX=3.7 EndY=-8 EndZ=0
    g7: LineSegment StartX=3.7 StartY=-8 StartZ=0 EndX=-3.7 EndY=-8 EndZ=0
  constraints (21):
    c: Coincident(g0,g1)
    c: Coincident(g1,g2)
    c: Coincident(g2,g3)
    c: Coincident(g3,g0)
    c: Vertical(g0)
    c: Vertical(g2)
    c: Coincident(g4,g5)
    c: Coincident(g5,g6)
    c: Coincident(g6,g7)
    c: Coincident(g7,g4)
    c: Vertical(g4)
    c: Vertical(g6)
    c: Horizontal(g5)
    c: Horizontal(g7)
    c: Symmetric(g0,g6,g-1)
    c: DistanceY(g-1,g1) = 8
    c: DistanceY(g2,g2) = 3.6
    c: DistanceX(g3,g3) = 7.4
    c: Symmetric(g2,g4,g-1)
    c: Symmetric(g1,g0,g-2)
    c: Horizontal(g3)
FEATURE [Sketcher::SketchObject] Sketch009
  ArcFitTolerance = 1e-06
  AttachmentSupport = -> [XY_Plane005]
  ExternalTypes = [0]
  FullyConstrained = true
  MakeInternals = false
  MapMode = 5
  _ExternalGeoVersion = 0
  sketch-geometry (1):
    g0: Circle CenterX=0 CenterY=-6 CenterZ=0 NormalX=0 NormalY=0 NormalZ=1 AngleXU=0 Radius=2.25
  constraints (3):
    c: PointOnObject(g0,g-2)
    c: Diameter(g0) = 4.5
    c: DistanceY(g0,g-1) = 6
FEATURE [Sketcher::SketchObject] Sketch010
  ArcFitTolerance = 1e-06
  AttachmentOffset = pos=(0,0,0) rot=(1,0,0;0.392699rad)
  AttachmentSupport = -> [YZ_Plane005]
  ExternalTypes = [0]
  FullyConstrained = true
  MakeInternals = false
  MapMode = 5
  Placement = pos=(0,0,0) rot=(0.639338,0.639338,0.427192;2.33414rad)
  _ExternalGeoVersion = 0
  sketch-geometry (4):
    g0: LineSegment StartX=-3 StartY=14.5 StartZ=0 EndX=-12 EndY=14.5 EndZ=0
    g1: LineSegment StartX=-12 StartY=14.5 StartZ=0 EndX=-5 EndY=44.5 EndZ=0
    g2: LineSegment StartX=-5 StartY=44.5 StartZ=0 EndX=-3 EndY=44.5 EndZ=0
    g3: LineSegment StartX=-3 StartY=44.5 StartZ=0 EndX=-3 EndY=14.5 EndZ=0
  constraints (12):
    c: Coincident(g0,g1)
    c: Coincident(g1,g2)
    c: Horizontal(g2)
    c: Coincident(g2,g3)
    c: Coincident(g3,g0)
    c: Horizontal(g0)
    c: Vertical(g3)
    c: DistanceX(g0,g-1) = 3
    c: DistanceY(g-1,g0) = 14.5
    c: DistanceY(g3,g3) = 30
    c: DistanceX(g2,g2) = 2
    c: DistanceX(g0,g0) = 9
FEATURE [Sketcher::SketchObject] Sketch011
  ArcFitTolerance = 1e-06
  AttachmentSupport = -> [XZ_Plane005]
  ExternalTypes = [0]
  FullyConstrained = true
  MakeInternals = false
  MapMode = 5
  Placement = pos=(0,0,0) rot=(1,0,0;1.5708rad)
  _ExternalGeoVersion = 0
  sketch-geometry (1):
    g0: Circle CenterX=0 CenterY=52 CenterZ=0 NormalX=0 NormalY=0 NormalZ=1 AngleXU=0 Radius=2.3
  constraints (3):
    c: PointOnObject(g0,g-2)
    c: Diameter(g0) = 4.6
    c: DistanceY(g-1,g0) = 52
FEATURE [Sketcher::SketchObject] Sketch012
  ArcFitTolerance = 1e-06
  AttachmentSupport = -> [XZ_Plane005]
  ExternalTypes = [0]
  FullyConstrained = true
  MakeInternals = false
  MapMode = 5
  Placement = pos=(0,0,0) rot=(1,0,0;1.5708rad)
  _ExternalGeoVersion = 0
  sketch-geometry (5):
    g0: LineSegment StartX=0 StartY=0 StartZ=0 EndX=-1.04189 EndY=5.90885 EndZ=0
    g1: LineSegment StartX=-1.04189 StartY=5.90885 StartZ=0 EndX=-0.2 EndY=5.3692 EndZ=0
    g2: LineSegment StartX=-0.2 StartY=5.3692 StartZ=0 EndX=0.2 EndY=5.3692 EndZ=0
    g3: LineSegment StartX=0.2 StartY=5.3692 StartZ=0 EndX=1.04189 EndY=5.90885 EndZ=0
    g4: LineSegment StartX=1.04189 StartY=5.90885 StartZ=0 EndX=0 EndY=0 EndZ=0
  constraints (13):
    c: Coincident(g-1,g0)
    c: Coincident(g0,g1)
    c: Coincident(g1,g2)
    c: Horizontal(g2)
    c: Coincident(g2,g3)
    c: Coincident(g3,g4)
    c: Coincident(g4,g0)
    c: Symmetric(g3,g0,g-2)
    c: Angle(g4,g0) = 0.349066
    c: DistanceX(g2,g2) = 0.4
    c: Distance(g4) = 6
    c: Distance(g3) = 1
    c: Distance(g1) = 1
FEATURE [Sketcher::SketchObject] Sketch013
  ArcFitTolerance = 1e-06
  AttachmentSupport = -> [XZ_Plane005]
  ExternalTypes = [0]
  FullyConstrained = true
  MakeInternals = false
  MapMode = 5
  Placement = pos=(0,0,0) rot=(1,0,0;1.5708rad)
  _ExternalGeoVersion = 0
  sketch-geometry (2):
    g0: Circle CenterX=0 CenterY=0 CenterZ=0 NormalX=0 NormalY=0 NormalZ=1 AngleXU=0 Radius=5
    g1: Circle CenterX=0 CenterY=0 CenterZ=0 NormalX=0 NormalY=0 NormalZ=1 AngleXU=0 Radius=15
  constraints (4):
    c: Coincident(g0,g-1)
    c: Coincident(g1,g0)
    c: Diameter(g1) = 30
    c: Diameter(g0) = 10
FEATURE [Sketcher::SketchObject] Sketch014
  ArcFitTolerance = 1e-06
  AttachmentSupport = -> [XZ_Plane005]
  ExternalTypes = [0]
  FullyConstrained = true
  MakeInternals = false
  MapMode = 5
  Placement = pos=(0,0,0) rot=(1,0,0;1.5708rad)
  _ExternalGeoVersion = 0
  sketch-geometry (6):
    g0: ArcOfCircle CenterX=0 CenterY=0 CenterZ=0 NormalX=0 NormalY=0 NormalZ=1 AngleXU=0 Radius=15 StartAngle=1.23918 EndAngle=1.90241
    g1: ArcOfCircle CenterX=0 CenterY=0 CenterZ=0 NormalX=0 NormalY=0 NormalZ=1 AngleXU=0 Radius=46 StartAngle=1.23918 EndAngle=1.90241
    g2: LineSegment [constr] StartX=0 StartY=0 StartZ=0 EndX=-19.5341 EndY=56.7311 EndZ=0
    g3: LineSegment [constr] StartX=0 StartY=0 StartZ=0 EndX=19.5341 EndY=56.7311 EndZ=0
    g4: LineSegment StartX=-4.88352 StartY=14.1828 StartZ=0 EndX=-14.9761 EndY=43.4939 EndZ=0
    g5: LineSegment StartX=14.9761 StartY=43.4939 StartZ=0 EndX=4.88352 EndY=14.1828 EndZ=0
  constraints (17):
    c: Coincident(g0,g-1)
    c: Coincident(g1,g0)
    c: Coincident(g2,g0)
    c: Coincident(g3,g0)
    c: Coincident(g4,g0)
    c: Coincident(g4,g1)
    c: Coincident(g5,g1)
    c: Coincident(g5,g0)
    c: Symmetric(g2,g3,g-2)
    c: Angle(g3,g2) = 0.663225
    c: PointOnObject(g0,g3)
    c: PointOnObject(g1,g3)
    c: PointOnObject(g0,g2)
    c: PointOnObject(g1,g2)
    c: Diameter(g1) = 92
    c: Diameter(g0) = 30
    c: Distance(g3) = 60
FEATURE [Sketcher::SketchObject] Sketch015
  ArcFitTolerance = 1e-06
  AttachmentSupport = -> [XZ_Plane005]
  ExternalTypes = [0]
  FullyConstrained = true
  MakeInternals = false
  MapMode = 5
  Placement = pos=(0,0,0) rot=(1,0,0;1.5708rad)
  _ExternalGeoVersion = 0
  sketch-geometry (2):
    g0: Circle CenterX=0 CenterY=0 CenterZ=0 NormalX=0 NormalY=0 NormalZ=1 AngleXU=0 Radius=58
    g1: Circle CenterX=0 CenterY=0 CenterZ=0 NormalX=0 NormalY=0 NormalZ=1 AngleXU=0 Radius=5
  constraints (4):
    c: Coincident(g0,g-1)
    c: Diameter(g0) = 116
    c: Coincident(g1,g0)
    c: Diameter(g1) = 10
FEATURE [PartDesign::Pad] Pad005  label="Pad_External"
  Direction = (0,-1,2e-16)
  Length = 3
  Length2 = 10
  Placement = pos=(0,0,0) rot=(1,0,0;1.5708rad)
  Profile = -> Sketch015
  ReferenceAxis = -> Sketch015 [N_Axis]
  Refine = true
  SideType = 0
  Suppressed = false
  Type = 0
  Type2 = 0
FEATURE [PartDesign::Pocket] Pocket002  label="Pocket_Gap"
  BaseFeature = -> Pad005
  Direction = (0,1,-2e-16)
  Length = 5
  Length2 = 5
  Placement = pos=(0,0,0) rot=(1,0,0;1.5708rad)
  Profile = -> Sketch014
  ReferenceAxis = -> Sketch014 [N_Axis]
  Refine = true
  Reversed = true
  SideType = 0
  Suppressed = false
  Type = 0
  Type2 = 0
FEATURE [PartDesign::PolarPattern] PolarPattern  label="PolarPattern_Gaps"
  Angle = 360
  Axis = -> Sketch014 [N_Axis]
  BaseFeature = -> Pocket002
  Mode = 0
  Occurrences = 8
  Offset = 120
  Originals = -> [Pocket002]
  Placement = pos=(0,0,0) rot=(1,0,0;1.5708rad)
  Refine = true
  SpacingPattern = [0]
  Spacings = [-1,-1,-1,-1,-1,-1,-1]
  Suppressed = false
  TransformMode = 0
FEATURE [PartDesign::Pad] Pad006  label="Pad_Center"
  BaseFeature = -> PolarPattern
  Direction = (0,-1,2e-16)
  Length = 12
  Length2 = 10
  Placement = pos=(0,0,0) rot=(1,0,0;1.5708rad)
  Profile = -> Sketch013
  ReferenceAxis = -> Sketch013 [N_Axis]
  Refine = true
  SideType = 0
  Suppressed = false
  Type = 0
  Type2 = 0
FEATURE [PartDesign::Pocket] Pocket003  label="Pocket_Shaft"
  BaseFeature = -> Pad006
  Direction = (0,1,-2e-16)
  Length = 5
  Length2 = 5
  Placement = pos=(0,0,0) rot=(1,0,0;1.5708rad)
  Profile = -> Sketch012
  ReferenceAxis = -> Sketch012 [N_Axis]
  Refine = true
  Reversed = true
  SideType = 0
  Suppressed = false
  Type = 1
  Type2 = 0
FEATURE [PartDesign::PolarPattern] PolarPattern001  label="PolarPattern_DriveShaft"
  Angle = 360
  Axis = -> Sketch012 [N_Axis]
  BaseFeature = -> Pocket003
  Mode = 0
  Occurrences = 18
  Offset = 120
  Originals = -> [Pocket003]
  Placement = pos=(0,0,0) rot=(1,0,0;1.5708rad)
  Refine = true
  SpacingPattern = [0]
  Spacings = [-1,-1,-1,-1,-1,-1,-1,-1,-1,-1,-1,-1,-1,-1,-1,-1,-1]
  Suppressed = false
  TransformMode = 0
FEATURE [PartDesign::Pocket] Pocket004  label="Pocket_Screw"
  BaseFeature = -> PolarPattern001
  Direction = (0,1,-2e-16)
  Length = 5
  Length2 = 5
  Placement = pos=(0,0,0) rot=(1,0,0;1.5708rad)
  Profile = -> Sketch011
  ReferenceAxis = -> Sketch011 [N_Axis]
  Refine = true
  Reversed = true
  SideType = 0
  Suppressed = false
  Type = 1
  Type2 = 0
FEATURE [PartDesign::PolarPattern] PolarPattern002  label="PolarPattern_Inertia"
  Angle = 360
  Axis = -> Sketch011 [N_Axis]
  BaseFeature = -> Pocket004
  Mode = 0
  Occurrences = 32
  Offset = 120
  Originals = -> [Pocket004]
  Placement = pos=(0,0,0) rot=(1,0,0;1.5708rad)
  Refine = true
  SpacingPattern = [0]
  Spacings = [-1,-1,-1,-1,-1,-1,-1,-1,-1,-1,-1,-1,-1,-1,-1,-1,-1,-1,-1,-1,-1,-1,-1,-1,-1,-1,-1,-1,-1,-1,-1]
  Suppressed = false
  TransformMode = 0
FEATURE [PartDesign::Pad] Pad007  label="Pad_Reinforcement"
  BaseFeature = -> PolarPattern002
  Direction = (0.92388,0,-0.382683)
  Length = 2
  Length2 = 10
  Placement = pos=(0,0,0) rot=(1,0,0;1.5708rad)
  Profile = -> Sketch010
  ReferenceAxis = -> Sketch010 [N_Axis]
  Refine = true
  SideType = 2
  Suppressed = false
  Type = 0
  Type2 = 0
FEATURE [PartDesign::PolarPattern] PolarPattern003  label="PolarPattern_Reinforcements"
  Angle = 360
  Axis = -> Y_Axis005
  BaseFeature = -> Pad007
  Mode = 0
  Occurrences = 8
  Offset = 120
  Originals = -> [Pad007]
  Placement = pos=(0,0,0) rot=(1,0,0;1.5708rad)
  Refine = true
  SpacingPattern = [0]
  Spacings = [-1,-1,-1,-1,-1,-1,-1]
  Suppressed = false
  TransformMode = 0
FEATURE [PartDesign::Pocket] Pocket005  label="Pocket_Fixation"
  BaseFeature = -> PolarPattern003
  Direction = (0,0,-1)
  Length = 30
  Length2 = 5
  Placement = pos=(0,0,0) rot=(1,0,0;1.5708rad)
  Profile = -> Sketch009
  ReferenceAxis = -> Sketch009 [N_Axis]
  Refine = true
  SideType = 2
  Suppressed = false
  Type = 0
  Type2 = 0
FEATURE [PartDesign::Pocket] Pocket006  label="Pocket_Bolts"
  BaseFeature = -> Pocket005
  Direction = (0,1,-2e-16)
  Length = 12
  Length2 = 5
  Placement = pos=(0,0,0) rot=(1,0,0;1.5708rad)
  Profile = -> Sketch008
  ReferenceAxis = -> Sketch008 [N_Axis]
  Refine = true
  Reversed = true
  SideType = 0
  Suppressed = false
  Type = 0
  Type2 = 0
FEATURE [PartDesign::Chamfer] Chamfer001
  Angle = 45
  Base = -> Pocket006 [Edge336,Edge335,Edge334,Edge333,Edge315,Edge311,Edge310,Edge292,Edge291,Edge284,Edge285,Edge283,Edge286,Edge287,Edge296,Edge297,Edge298,Edge299,Edge300,Edge301,Edge305,Edge309,Edge342,Edge343,Edge344,Edge351,Edge350,Edge352,Edge349,Edge348,Edge338,Edge337]
  BaseFeature = -> Pocket006
  ChamferType = 0
  FlipDirection = true
  Placement = pos=(0,0,0) rot=(1,0,0;1.5708rad)
  Refine = true
  Size = 1.5
  Size2 = 1
  SupportTransform = false
  Suppressed = false
  UseAllEdges = false
FEATURE [PartDesign::CoordinateSystem] reactionWheel
  AttacherType = Attacher::AttachEngine3D
  AttachmentOffset = pos=(0,0,0) rot=(-0.57735,0.57735,-0.57735;2.0944rad)
  AttachmentSupport = -> [Chamfer001]
  MapMode = 11
  Placement = pos=(0,-12,5.3e-15) rot=(0,0,1;0rad)
FEATURE [PartDesign::Body] Body004  label="Body_ReactionWheel"
  AllowCompound = false
  Group = -> [Sketch015,Pad005,Sketch014,Pocket002,PolarPattern,Sketch013,Pad006,Sketch012,Pocket003,PolarPattern001,Sketch011,Pocket004,PolarPattern002,Sketch010,Pad007,PolarPattern003,Sketch009,Pocket005,Sketch008,Pocket006,reactionWheel,Chamfer001]
  Origin = -> Origin005
  Tip = -> Chamfer001
COMPONENT P4 — recipe-attached ("Body_Motor", modeled in this document).
Construction recipe (the document's own serialized feature program — sketch geometry with constraints, then the solid features built on it; lengths are millimeters unless a unit is written):

FEATURE [Sketcher::SketchObject] Sketch016
  ArcFitTolerance = 1e-06
  AttachmentSupport = -> [XY_Plane006]
  ExternalTypes = [0]
  FullyConstrained = true
  MakeInternals = false
  MapMode = 5
  _ExternalGeoVersion = 0
  sketch-geometry (8):
    g0: LineSegment StartX=-7.5 StartY=-8 StartZ=0 EndX=-7.5 EndY=-13 EndZ=0
    g1: LineSegment StartX=7.5 StartY=-13 StartZ=0 EndX=7.5 EndY=-8 EndZ=0
    g2: LineSegment StartX=7.5 StartY=-8 StartZ=0 EndX=-7.5 EndY=-8 EndZ=0
    g3: LineSegment StartX=-10 StartY=-13 StartZ=0 EndX=-10 EndY=-14.2 EndZ=0
    g4: LineSegment StartX=-10 StartY=-14.2 StartZ=0 EndX=10 EndY=-14.2 EndZ=0
    g5: LineSegment StartX=10 StartY=-14.2 StartZ=0 EndX=10 EndY=-13 EndZ=0
    g6: LineSegment StartX=10 StartY=-13 StartZ=0 EndX=7.5 EndY=-13 EndZ=0
    g7: LineSegment StartX=-7.5 StartY=-13 StartZ=0 EndX=-10 EndY=-13 EndZ=0
  constraints (21):
    c: Coincident(g1,g2)
    c: Coincident(g2,g0)
    c: Vertical(g0)
    c: Coincident(g3,g4)
    c: Coincident(g4,g5)
    c: Coincident(g5,g6)
    c: Coincident(g7,g3)
    c: Vertical(g3)
    c: Vertical(g5)
    c: Horizontal(g6)
    c: Coincident(g6,g1)
    c: Coincident(g0,g7)
    c: Symmetric(g0,g1,g-2)
    c: Symmetric(g3,g4,g-2)
    c: Symmetric(g0,g1,g-2)
    c: DistanceX(g2,g2) = 15
    c: DistanceX(g4,g4) = 20
    c: DistanceY(g3,g3) = 1.2
    c: Horizontal(g7)
    c: DistanceY(g0,g0) = 5
    c: DistanceY(g0,g-1) = 8
FEATURE [Sketcher::SketchObject] Sketch017
  ArcFitTolerance = 1e-06
  AttachmentOffset = pos=(0,0,42) rot=(0,0,1;0rad)
  AttachmentSupport = -> [XZ_Plane006]
  ExternalTypes = [0]
  FullyConstrained = true
  MakeInternals = false
  MapMode = 5
  Placement = pos=(0,-42,9.3e-15) rot=(1,0,0;1.5708rad)
  _ExternalGeoVersion = 0
  sketch-geometry (5):
    g0: LineSegment StartX=-0.955065 StartY=5.41644 StartZ=0 EndX=0 EndY=0 EndZ=0
    g1: LineSegment StartX=0.955065 StartY=5.41644 StartZ=0 EndX=0 EndY=0 EndZ=0
    g2: LineSegment StartX=-0.955065 StartY=5.41644 StartZ=0 EndX=-0.2 EndY=4.76079 EndZ=0
    g3: LineSegment StartX=-0.2 StartY=4.76079 StartZ=0 EndX=0.2 EndY=4.76079 EndZ=0
    g4: LineSegment StartX=0.2 StartY=4.76079 StartZ=0 EndX=0.955065 EndY=5.41644 EndZ=0
  constraints (12):
    c: Coincident(g0,g-1)
    c: Coincident(g1,g0)
    c: Coincident(g3,g2)
    c: Coincident(g4,g3)
    c: Coincident(g4,g1)
    c: Symmetric(g3,g2,g-2)
    c: Coincident(g2,g0)
    c: Symmetric(g0,g1,g-2)
    c: Angle(g1,g0) = 0.349066
    c: DistanceX(g3,g3) = 0.4
    c: Distance(g1) = 5.5
    c: Distance(g4) = 1
FEATURE [Sketcher::SketchObject] Sketch018
  ArcFitTolerance = 1e-06
  AttachmentSupport = -> [XZ_Plane006]
  ExternalTypes = [0]
  FullyConstrained = true
  MakeInternals = false
  MapMode = 5
  Placement = pos=(0,0,0) rot=(1,0,0;1.5708rad)
  _ExternalGeoVersion = 0
  sketch-geometry (1):
    g0: Circle CenterX=0 CenterY=0 CenterZ=0 NormalX=0 NormalY=0 NormalZ=1 AngleXU=0 Radius=21
  constraints (2):
    c: Coincident(g0,g-1)
    c: Diameter(g0) = 42
FEATURE [PartDesign::Pad] Pad008  label="Pad_Cylinder"
  Direction = (0,-1,2e-16)
  Length = 34
  Length2 = 10
  Placement = pos=(0,0,0) rot=(1,0,0;1.5708rad)
  Profile = -> Sketch018
  ReferenceAxis = -> Sketch018 [N_Axis]
  Refine = true
  SideType = 0
  Suppressed = false
  Type = 0
  Type2 = 0
FEATURE [Sketcher::SketchObject] Sketch019
  ArcFitTolerance = 1e-06
  AttachmentSupport = -> [Pad008]
  ExternalTypes = [0]
  FullyConstrained = true
  MakeInternals = false
  MapMode = 5
  Placement = pos=(0,-34,0) rot=(1,0,0;1.5708rad)
  _ExternalGeoVersion = 0
  sketch-geometry (1):
    g0: Circle CenterX=0 CenterY=0 CenterZ=0 NormalX=0 NormalY=0 NormalZ=1 AngleXU=0 Radius=7.5
  constraints (2):
    c: Coincident(g0,g-1)
    c: Diameter(g0) = 15
FEATURE [PartDesign::Pad] Pad009  label="Pad_Bearing"
  BaseFeature = -> Pad008
  Direction = (0,-1,2e-16)
  Length = 1.2
  Length2 = 10
  Placement = pos=(0,0,0) rot=(1,0,0;1.5708rad)
  Profile = -> Sketch019
  ReferenceAxis = -> Sketch019 [N_Axis]
  Refine = true
  SideType = 0
  Suppressed = false
  Type = 0
  Type2 = 0
FEATURE [Sketcher::SketchObject] Sketch020
  ArcFitTolerance = 1e-06
  AttachmentSupport = -> [Pad009]
  ExternalTypes = [0]
  FullyConstrained = true
  MakeInternals = false
  MapMode = 5
  Placement = pos=(0,-35.2,0) rot=(1,0,0;1.5708rad)
  _ExternalGeoVersion = 0
  sketch-geometry (1):
    g0: Circle CenterX=0 CenterY=0 CenterZ=0 NormalX=0 NormalY=0 NormalZ=1 AngleXU=0 Radius=3
  constraints (2):
    c: Coincident(g0,g-1)
    c: Diameter(g0) = 6
FEATURE [PartDesign::Pad] Pad010  label="Pad_Drive_Shaft"
  BaseFeature = -> Pad009
  Direction = (0,-1,2e-16)
  Length = 6.4
  Length2 = 10
  Placement = pos=(0,0,0) rot=(1,0,0;1.5708rad)
  Profile = -> Sketch020
  ReferenceAxis = -> Sketch020 [N_Axis]
  Refine = true
  SideType = 0
  Suppressed = false
  Type = 0
  Type2 = 0
FEATURE [Sketcher::SketchObject] Sketch021
  ArcFitTolerance = 1e-06
  AttachmentSupport = -> [Pad010]
  ExternalTypes = [0]
  FullyConstrained = true
  MakeInternals = false
  MapMode = 5
  Placement = pos=(0,-41.6,0) rot=(1,0,0;1.5708rad)
  _ExternalGeoVersion = 0
  sketch-geometry (1):
    g0: Circle CenterX=0 CenterY=0 CenterZ=0 NormalX=0 NormalY=0 NormalZ=1 AngleXU=0 Radius=7.5
  constraints (2):
    c: Coincident(g0,g-1)
    c: Diameter(g0) = 15
FEATURE [PartDesign::Pad] Pad011  label="Pad_Thrust001"
  BaseFeature = -> Pad010
  Direction = (0,-1,2e-16)
  Length = 1.3
  Length2 = 10
  Placement = pos=(0,0,0) rot=(1,0,0;1.5708rad)
  Profile = -> Sketch021
  ReferenceAxis = -> Sketch021 [N_Axis]
  Refine = true
  SideType = 0
  Suppressed = false
  Type = 0
  Type2 = 0
FEATURE [PartDesign::Pad] Pad012  label="Pad_Tooth"
  BaseFeature = -> Pad011
  Direction = (0,-1,2e-16)
  Length = 12
  Length2 = 10
  Placement = pos=(0,0,0) rot=(1,0,0;1.5708rad)
  Profile = -> Sketch017
  ReferenceAxis = -> Sketch017 [N_Axis]
  Refine = true
  SideType = 0
  Suppressed = false
  Type = 0
  Type2 = 0
FEATURE [PartDesign::PolarPattern] PolarPattern004  label="PolarPattern_Shaft"
  Angle = 360
  Axis = -> Sketch017 [N_Axis]
  BaseFeature = -> Pad012
  Mode = 0
  Occurrences = 18
  Offset = 120
  Originals = -> [Pad012]
  Placement = pos=(0,0,0) rot=(1,0,0;1.5708rad)
  Refine = true
  SpacingPattern = [0]
  Spacings = [-1,-1,-1,-1,-1,-1,-1,-1,-1,-1,-1,-1,-1,-1,-1,-1,-1]
  Suppressed = false
  TransformMode = 0
FEATURE [Sketcher::SketchObject] Sketch022
  ArcFitTolerance = 1e-06
  AttachmentSupport = -> [PolarPattern004]
  ExternalTypes = [0]
  FullyConstrained = true
  MakeInternals = false
  MapMode = 5
  Placement = pos=(0,-34,0) rot=(1,0,0;1.5708rad)
  _ExternalGeoVersion = 0
  sketch-geometry (1):
    g0: Circle CenterX=0 CenterY=15 CenterZ=0 NormalX=0 NormalY=0 NormalZ=1 AngleXU=0 Radius=1.75
  constraints (3):
    c: PointOnObject(g0,g-2)
    c: Diameter(g0) = 3.5
    c: DistanceY(g-1,g0) = 15
FEATURE [PartDesign::Pocket] Pocket007  label="Pocket_Screw001"
  BaseFeature = -> PolarPattern004
  Direction = (0,1,-2e-16)
  Length = 5
  Length2 = 5
  Placement = pos=(0,0,0) rot=(1,0,0;1.5708rad)
  Profile = -> Sketch022
  ReferenceAxis = -> Sketch022 [N_Axis]
  Refine = true
  SideType = 0
  Suppressed = false
  Type = 0
  Type2 = 0
FEATURE [PartDesign::PolarPattern] PolarPattern005  label="PolarPattern_Fixations"
  Angle = 360
  Axis = -> Sketch022 [N_Axis]
  BaseFeature = -> Pocket007
  Mode = 0
  Occurrences = 3
  Offset = 120
  Originals = -> [Pocket007]
  Placement = pos=(0,0,0) rot=(1,0,0;1.5708rad)
  Refine = true
  SpacingPattern = [0]
  Spacings = [-1,-1]
  Suppressed = false
  TransformMode = 0
FEATURE [PartDesign::Pad] Pad013  label="Pad_Connector"
  BaseFeature = -> PolarPattern005
  Direction = (0,0,1)
  Length = 22
  Length2 = 10
  Placement = pos=(0,0,0) rot=(1,0,0;1.5708rad)
  Profile = -> Sketch016
  ReferenceAxis = -> Sketch016 [N_Axis]
  Refine = true
  Reversed = true
  SideType = 0
  Suppressed = false
  Type = 0
  Type2 = 0
FEATURE [Sketcher::SketchObject] Sketch023
  ArcFitTolerance = 1e-06
  AttachmentSupport = -> [Pad013]
  ExternalGeometry = -> [Pad013]
  ExternalTypes = [0]
  FullyConstrained = true
  MakeInternals = false
  MapMode = 5
  Placement = pos=(0,0,-22) rot=(1,0,0;3.14159rad)
  _ExternalGeoVersion = 0
  sketch-geometry (4):
    g0: LineSegment StartX=-6.5 StartY=12 StartZ=0 EndX=-6.5 EndY=9 EndZ=0
    g1: LineSegment StartX=-6.5 StartY=9 StartZ=0 EndX=6.5 EndY=9 EndZ=0
    g2: LineSegment StartX=6.5 StartY=9 StartZ=0 EndX=6.5 EndY=12 EndZ=0
    g3: LineSegment StartX=6.5 StartY=12 StartZ=0 EndX=-6.5 EndY=12 EndZ=0
  constraints (12):
    c: Coincident(g0,g1)
    c: Coincident(g1,g2)
    c: Coincident(g2,g3)
    c: Coincident(g3,g0)
    c: Vertical(g0)
    c: Vertical(g2)
    c: Horizontal(g1)
    c: Horizontal(g3)
    c: DistanceX(g-3,g0) = 1
    c: DistanceX(g1,g-4) = 1
    c: DistanceY(g-4,g1) = 1
    c: DistanceY(g0,g-3) = 1
FEATURE [PartDesign::Pocket] Pocket008  label="Pocket_Pins"
  BaseFeature = -> Pad013
  Direction = (0,0,1)
  Length = 5
  Length2 = 5
  Placement = pos=(0,0,0) rot=(1,0,0;1.5708rad)
  Profile = -> Sketch023
  ReferenceAxis = -> Sketch023 [N_Axis]
  Refine = true
  SideType = 0
  Suppressed = false
  Type = 0
  Type2 = 0
FEATURE [PartDesign::Fillet] Fillet001  label="Fillet_Cylinder"
  Base = -> Pocket008 [Edge3,Edge1]
  BaseFeature = -> Pocket008
  Placement = pos=(0,0,0) rot=(1,0,0;1.5708rad)
  Radius = 3
  Refine = true
  SupportTransform = false
  Suppressed = false
  UseAllEdges = false
FEATURE [PartDesign::Fillet] Fillet002  label="Fillet_Thrust_Bearing"
  Base = -> Fillet001 [Edge61,Edge43]
  BaseFeature = -> Fillet001
  Placement = pos=(0,0,0) rot=(1,0,0;1.5708rad)
  Radius = 1
  Refine = true
  SupportTransform = false
  Suppressed = false
  UseAllEdges = false
FEATURE [PartDesign::CoordinateSystem] Motor
  AttacherType = Attacher::AttachEngine3D
  AttachmentOffset = pos=(0,0,0) rot=(-0.57735,0.57735,-0.57735;2.0944rad)
  AttachmentSupport = -> [Fillet002]
  MapMode = 11
  Placement = pos=(0,-34,15) rot=(0,0,1;0rad)
FEATURE [PartDesign::CoordinateSystem] Motor_Shaft001
  AttacherType = Attacher::AttachEngine3D
  AttachmentOffset = pos=(0,0,0) rot=(-0.57735,0.57735,-0.57735;2.0944rad)
  AttachmentSupport = -> [Fillet002]
  MapMode = 11
  Placement = pos=(0,-42.9,9.5e-15) rot=(0,0,1;0rad)
FEATURE [PartDesign::Body] Body005  label="Body_Motor"
  AllowCompound = false
  Group = -> [Sketch018,Pad008,Sketch019,Pad009,Sketch020,Pad010,Sketch021,Pad011,Sketch017,Pad012,PolarPattern004,Sketch022,Pocket007,PolarPattern005,Sketch016,Pad013,Sketch023,Pocket008,Fillet001,Fillet002,Motor,Motor_Shaft001]
  Origin = -> Origin006
  Tip = -> Fillet002
COMPONENT P5 — recipe-attached ("Body_MPU6050", modeled in this document).
Construction recipe (the document's own serialized feature program — sketch geometry with constraints, then the solid features built on it; lengths are millimeters unless a unit is written):

FEATURE [Sketcher::SketchObject] Sketch024
  ArcFitTolerance = 1e-06
  AttachmentSupport = -> [XZ_Plane008]
  ExternalTypes = [0]
  FullyConstrained = true
  MakeInternals = false
  MapMode = 5
  Placement = pos=(0,0,0) rot=(1,0,0;1.5708rad)
  _ExternalGeoVersion = 0
  sketch-geometry (76):
    g0: LineSegment StartX=-8.94 StartY=-2.15 StartZ=0 EndX=-11.04 EndY=-2.15 EndZ=0
    g1: LineSegment StartX=-11.04 StartY=-2.15 StartZ=0 EndX=-11.04 EndY=-3.15 EndZ=0
    g2: LineSegment StartX=-11.04 StartY=-3.15 StartZ=0 EndX=-8.94 EndY=-3.15 EndZ=0
    g3: LineSegment StartX=-8.94 StartY=-3.15 StartZ=0 EndX=-8.94 EndY=-2.15 EndZ=0
    g4: LineSegment StartX=-8.94 StartY=-3.65 StartZ=0 EndX=-11.04 EndY=-3.65 EndZ=0
    g5: LineSegment StartX=-11.04 StartY=-3.65 StartZ=0 EndX=-11.04 EndY=-4.65 EndZ=0
    g6: LineSegment StartX=-11.04 StartY=-4.65 StartZ=0 EndX=-8.94 EndY=-4.65 EndZ=0
    g7: LineSegment StartX=-8.94 StartY=-4.65 StartZ=0 EndX=-8.94 EndY=-3.65 EndZ=0
    g8: LineSegment StartX=-8.94 StartY=-5.15 StartZ=0 EndX=-11.04 EndY=-5.15 EndZ=0
    g9: LineSegment StartX=-11.04 StartY=-5.15 StartZ=0 EndX=-11.04 EndY=-6.15 EndZ=0
    g10: LineSegment StartX=-11.04 StartY=-6.15 StartZ=0 EndX=-8.94 EndY=-6.15 EndZ=0
    g11: LineSegment StartX=-8.94 StartY=-6.15 StartZ=0 EndX=-8.94 EndY=-5.15 EndZ=0
    g12: LineSegment StartX=-5.34 StartY=-3.65 StartZ=0 EndX=-7.44 EndY=-3.65 EndZ=0
    g13: LineSegment StartX=-7.44 StartY=-3.65 StartZ=0 EndX=-7.44 EndY=-4.65 EndZ=0
    g14: LineSegment StartX=-7.44 StartY=-4.65 StartZ=0 EndX=-5.34 EndY=-4.65 EndZ=0
    g15: LineSegment StartX=-5.34 StartY=-4.65 StartZ=0 EndX=-5.34 EndY=-3.65 EndZ=0
    g16: LineSegment StartX=-5.34 StartY=-5.15 StartZ=0 EndX=-7.44 EndY=-5.15 EndZ=0
    g17: LineSegment StartX=-7.44 StartY=-5.15 StartZ=0 EndX=-7.44 EndY=-6.15 EndZ=0
    g18: LineSegment StartX=-7.44 StartY=-6.15 StartZ=0 EndX=-5.34 EndY=-6.15 EndZ=0
    g19: LineSegment StartX=-5.34 StartY=-6.15 StartZ=0 EndX=-5.34 EndY=-5.15 EndZ=0
    g20: LineSegment StartX=-1.68 StartY=-9.16 StartZ=0 EndX=-3.06 EndY=-9.16 EndZ=0
    g21: LineSegment StartX=-3.06 StartY=-9.16 StartZ=0 EndX=-3.06 EndY=-13.54 EndZ=0
    g22: LineSegment StartX=-3.06 StartY=-13.54 StartZ=0 EndX=-1.68 EndY=-13.54 EndZ=0
    g23: LineSegment StartX=-1.68 StartY=-13.54 StartZ=0 EndX=-1.68 EndY=-9.16 EndZ=0
    g24: LineSegment StartX=-4.18 StartY=-6.8 StartZ=0 EndX=-11.54 EndY=-6.8 EndZ=0
    g25: LineSegment StartX=-11.54 StartY=-6.8 StartZ=0 EndX=-11.54 EndY=-14.14 EndZ=0
    g26: LineSegment StartX=-11.54 StartY=-14.14 StartZ=0 EndX=-4.18 EndY=-14.14 EndZ=0
    g27: LineSegment StartX=-4.18 StartY=-14.14 StartZ=0 EndX=-4.18 EndY=-6.8 EndZ=0
    g28: LineSegment StartX=-4 StartY=-15.5 StartZ=0 EndX=-7.4 EndY=-15.5 EndZ=0
    g29: LineSegment StartX=-7.4 StartY=-15.5 StartZ=0 EndX=-7.4 EndY=-15.96 EndZ=0
    g30: LineSegment StartX=-7.4 StartY=-15.96 StartZ=0 EndX=-4 EndY=-15.96 EndZ=0
    g31: LineSegment StartX=-4 StartY=-15.96 StartZ=0 EndX=-4 EndY=-15.5 EndZ=0
    g32: LineSegment StartX=-8.9 StartY=-15.5 StartZ=0 EndX=-12.3 EndY=-15.5 EndZ=0
    g33: LineSegment StartX=-12.3 StartY=-15.5 StartZ=0 EndX=-12.3 EndY=-15.96 EndZ=0
    g34: LineSegment StartX=-12.3 StartY=-15.96 StartZ=0 EndX=-8.9 EndY=-15.96 EndZ=0
    g35: LineSegment StartX=-8.9 StartY=-15.96 StartZ=0 EndX=-8.9 EndY=-15.5 EndZ=0
    g36: LineSegment StartX=-8.9 StartY=-16.11 StartZ=0 EndX=-12.3 EndY=-16.11 EndZ=0
    g37: LineSegment StartX=-12.3 StartY=-16.11 StartZ=0 EndX=-12.3 EndY=-16.81 EndZ=0
    g38: LineSegment StartX=-12.3 StartY=-16.81 StartZ=0 EndX=-8.9 EndY=-16.81 EndZ=0
    g39: LineSegment StartX=-8.9 StartY=-16.81 StartZ=0 EndX=-8.9 EndY=-16.11 EndZ=0
    g40: LineSegment StartX=-4 StartY=-16.11 StartZ=0 EndX=-7.4 EndY=-16.11 EndZ=0
    g41: LineSegment StartX=-7.4 StartY=-16.11 StartZ=0 EndX=-7.4 EndY=-16.81 EndZ=0
    g42: LineSegment StartX=-7.4 StartY=-16.81 StartZ=0 EndX=-4 EndY=-16.81 EndZ=0
    g43: LineSegment StartX=-4 StartY=-16.81 StartZ=0 EndX=-4 EndY=-16.11 EndZ=0
    g44: LineSegment StartX=-4.78 StartY=-17.8 StartZ=0 EndX=-5.58 EndY=-17.8 EndZ=0
    g45: LineSegment StartX=-5.58 StartY=-17.8 StartZ=0 EndX=-5.58 EndY=-20.1 EndZ=0
    g46: LineSegment StartX=-5.58 StartY=-20.1 StartZ=0 EndX=-4.78 EndY=-20.1 EndZ=0
    g47: LineSegment StartX=-4.78 StartY=-20.1 StartZ=0 EndX=-4.78 EndY=-17.8 EndZ=0
    g48: LineSegment StartX=-10.88 StartY=-17.8 StartZ=0 EndX=-11.68 EndY=-17.8 EndZ=0
    g49: LineSegment StartX=-11.68 StartY=-17.8 StartZ=0 EndX=-11.68 EndY=-20.1 EndZ=0
    g50: LineSegment StartX=-11.68 StartY=-20.1 StartZ=0 EndX=-10.88 EndY=-20.1 EndZ=0
    g51: LineSegment StartX=-10.88 StartY=-20.1 StartZ=0 EndX=-10.88 EndY=-17.8 EndZ=0
    g52: LineSegment StartX=-6.28 StartY=-17.8 StartZ=0 EndX=-6.73 EndY=-17.8 EndZ=0
    g53: LineSegment StartX=-6.73 StartY=-18.12 StartZ=0 EndX=-6.28 EndY=-18.12 EndZ=0
    g54: LineSegment StartX=-6.28 StartY=-18.12 StartZ=0 EndX=-6.28 EndY=-17.8 EndZ=0
    g55: LineSegment StartX=-6.28 StartY=-19.72 StartZ=0 EndX=-6.73 EndY=-19.72 EndZ=0
    g56: LineSegment StartX=-6.73 StartY=-20.04 StartZ=0 EndX=-6.28 EndY=-20.04 EndZ=0
    g57: LineSegment StartX=-6.28 StartY=-20.04 StartZ=0 EndX=-6.28 EndY=-19.72 EndZ=0
    g58: LineSegment StartX=-9.17 StartY=-17.915 StartZ=0 EndX=-9.95 EndY=-17.915 EndZ=0
    g59: LineSegment StartX=-9.95 StartY=-17.915 StartZ=0 EndX=-9.95 EndY=-18.275 EndZ=0
    g60: LineSegment StartX=-9.95 StartY=-18.275 StartZ=0 EndX=-9.17 EndY=-18.275 EndZ=0
    g61: LineSegment StartX=-9.17 StartY=-18.74 StartZ=0 EndX=-9.95 EndY=-18.74 EndZ=0
    g62: LineSegment StartX=-9.95 StartY=-18.74 StartZ=0 EndX=-9.95 EndY=-19.1 EndZ=0
    g63: LineSegment StartX=-9.95 StartY=-19.1 StartZ=0 EndX=-9.17 EndY=-19.1 EndZ=0
    g64: LineSegment StartX=-9.17 StartY=-19.565 StartZ=0 EndX=-9.95 EndY=-19.565 EndZ=0
    g65: LineSegment StartX=-9.95 StartY=-19.565 StartZ=0 EndX=-9.95 EndY=-19.925 EndZ=0
    g66: LineSegment StartX=-9.95 StartY=-19.925 StartZ=0 EndX=-9.17 EndY=-19.925 EndZ=0
    g67: LineSegment StartX=-6.73 StartY=-17.45 StartZ=0 EndX=-9.17 EndY=-17.45 EndZ=0
    g68: LineSegment StartX=-9.17 StartY=-17.45 StartZ=0 EndX=-9.17 EndY=-17.915 EndZ=0
    g69: LineSegment StartX=-9.17 StartY=-20.39 StartZ=0 EndX=-6.73 EndY=-20.39 EndZ=0
    g70: LineSegment StartX=-6.73 StartY=-20.39 StartZ=0 EndX=-6.73 EndY=-20.04 EndZ=0
    g71: LineSegment StartX=-6.73 StartY=-17.8 StartZ=0 EndX=-6.73 EndY=-17.45 EndZ=0
    g72: LineSegment StartX=-6.73 StartY=-19.72 StartZ=0 EndX=-6.73 EndY=-18.12 EndZ=0
    g73: LineSegment StartX=-9.17 StartY=-18.275 StartZ=0 EndX=-9.17 EndY=-18.74 EndZ=0
    g74: LineSegment StartX=-9.17 StartY=-19.1 StartZ=0 EndX=-9.17 EndY=-19.565 EndZ=0
    g75: LineSegment StartX=-9.17 StartY=-19.925 StartZ=0 EndX=-9.17 EndY=-20.39 EndZ=0
  constraints (228):
    c: Coincident(g0,g1)
    c: Coincident(g1,g2)
    c: Coincident(g2,g3)
    c: Coincident(g3,g0)
    c: Horizontal(g0)
    c: Horizontal(g2)
    c: Vertical(g1)
    c: Vertical(g3)
    c: Coincident(g4,g5)
    c: Coincident(g5,g6)
    c: Coincident(g6,g7)
    c: Coincident(g7,g4)
    c: Horizontal(g4)
    c: Horizontal(g6)
    c: Vertical(g5)
    c: Vertical(g7)
    c: Coincident(g8,g9)
    c: Coincident(g9,g10)
    c: Coincident(g10,g11)
    c: Coincident(g11,g8)
    c: Horizontal(g8)
    c: Horizontal(g10)
    c: Vertical(g9)
    c: Vertical(g11)
    c: Coincident(g12,g13)
    c: Coincident(g13,g14)
    c: Coincident(g14,g15)
    c: Coincident(g15,g12)
    c: Horizontal(g12)
    c: Horizontal(g14)
    c: Vertical(g13)
    c: Vertical(g15)
    c: Coincident(g16,g17)
    c: Coincident(g17,g18)
    c: Coincident(g18,g19)
    c: Coincident(g19,g16)
    c: Horizontal(g16)
    c: Horizontal(g18)
    c: Vertical(g17)
    c: Vertical(g19)
    c: Coincident(g20,g21)
    c: Coincident(g21,g22)
    c: Coincident(g22,g23)
    c: Coincident(g23,g20)
    c: Horizontal(g20)
    c: Horizontal(g22)
    c: Vertical(g21)
    c: Vertical(g23)
    c: Coincident(g24,g25)
    c: Coincident(g25,g26)
    c: Coincident(g26,g27)
    c: Coincident(g27,g24)
    c: Horizontal(g24)
    c: Horizontal(g26)
    c: Vertical(g25)
    c: Vertical(g27)
    c: Coincident(g28,g29)
    c: Coincident(g29,g30)
    c: Coincident(g30,g31)
    c: Coincident(g31,g28)
    c: Horizontal(g28)
    c: Horizontal(g30)
    c: Vertical(g29)
    c: Vertical(g31)
    c: Coincident(g32,g33)
    c: Coincident(g33,g34)
    c: Coincident(g34,g35)
    c: Coincident(g35,g32)
    c: Horizontal(g32)
    c: Horizontal(g34)
    c: Vertical(g33)
    c: Vertical(g35)
    c: Coincident(g36,g37)
    c: Coincident(g37,g38)
    c: Coincident(g38,g39)
    c: Coincident(g39,g36)
    c: Horizontal(g36)
    c: Horizontal(g38)
    c: Vertical(g37)
    c: Vertical(g39)
    c: Coincident(g40,g41)
    c: Coincident(g41,g42)
    c: Coincident(g42,g43)
    c: Coincident(g43,g40)
    c: Horizontal(g40)
    c: Horizontal(g42)
    c: Vertical(g41)
    c: Vertical(g43)
    c: Coincident(g44,g45)
    c: Coincident(g45,g46)
    c: Coincident(g46,g47)
    c: Coincident(g47,g44)
    c: Horizontal(g44)
    c: Horizontal(g46)
    c: Vertical(g45)
    c: Vertical(g47)
    c: Coincident(g48,g49)
    c: Coincident(g49,g50)
    c: Coincident(g50,g51)
    c: Coincident(g51,g48)
    c: Horizontal(g48)
    c: Horizontal(g50)
    c: Vertical(g49)
    c: Vertical(g51)
    c: Coincident(g53,g54)
    c: Coincident(g54,g52)
    c: Horizontal(g52)
    c: Horizontal(g53)
    c: Vertical(g54)
    c: Coincident(g56,g57)
    c: Coincident(g57,g55)
    c: Horizontal(g55)
    c: Horizontal(g56)
    c: Vertical(g57)
    c: Coincident(g58,g59)
    c: Coincident(g59,g60)
    c: Horizontal(g58)
    c: Horizontal(g60)
    c: Vertical(g59)
    c: Coincident(g61,g62)
    c: Coincident(g62,g63)
    c: Horizontal(g61)
    c: Horizontal(g63)
    c: Vertical(g62)
    c: Coincident(g64,g65)
    c: Coincident(g65,g66)
    c: Horizontal(g64)
    c: Horizontal(g66)
    c: Vertical(g65)
    c: Coincident(g67,g68)
    c: Coincident(g75,g69)
    c: Coincident(g69,g70)
    c: Coincident(g71,g67)
    c: Horizontal(g67)
    c: Horizontal(g69)
    c: Vertical(g68)
    c: Vertical(g70)
    c: Equal(g0,g4)
    c: Equal(g4,g8)
    c: Equal(g8,g16)
    c: Equal(g16,g12)
    c: Equal(g19,g11)
    c: Equal(g11,g15)
    c: Equal(g15,g7)
    c: Equal(g7,g3)
    c: DistanceX(g0,g0) = 2.1
    c: DistanceY(g1,g1) = 1
    c: DistanceX(g0,g-1) = 8.94
    c: DistanceX(g4,g12) = 1.5
    c: DistanceY(g4,g1) = 0.5
    c: DistanceY(g8,g5) = 0.5
    c: PointOnObject(g17,g10)
    c: PointOnObject(g13,g6)
    c: PointOnObject(g13,g17)
    c: PointOnObject(g6,g11)
    c: DistanceY(g0,g-1) = 2.15
    c: PointOnObject(g4,g3)
    c: DistanceX(g24,g24) = 7.36
    c: DistanceY(g27,g27) = 7.34
    c: DistanceX(g24,g-1) = 4.18
    c: DistanceY(g24,g-1) = 6.8
    c: DistanceX(g20,g20) = 1.38
    c: DistanceY(g23,g23) = 4.38
    c: DistanceX(g20,g-1) = 1.68
    c: DistanceY(g20,g-1) = 9.16
    c: Equal(g28,g40)
    c: Equal(g40,g32)
    c: Equal(g32,g36)
    c: Equal(g29,g35)
    c: Equal(g43,g39)
    c: PointOnObject(g30,g43)
    c: PointOnObject(g34,g39)
    c: PointOnObject(g40,g36)
    c: PointOnObject(g29,g34)
    c: DistanceX(g28,g28) = 3.4
    c: DistanceY(g31,g31) = 0.46
    c: DistanceY(g40,g30) = 0.15
    c: DistanceY(g43,g43) = 0.7
    c: DistanceX(g32,g28) = 1.5
    c: DistanceX(g28,g-1) = 4
    c: DistanceY(g28,g-1) = 15.5
    c: Equal(g44,g48)
    c: Equal(g47,g51)
    c: PointOnObject(g44,g48)
    c: DistanceX(g46,g46) = 0.8
    c: DistanceY(g47,g47) = 2.3
    c: DistanceX(g46,g-1) = 4.78
    c: DistanceY(g44,g-1) = 17.8
    c: DistanceX(g50,g45) = 5.3
    c: Coincident(g72,g55)
    c: Coincident(g56,g70)
    c: Vertical(g72)
    c: PointOnObject(g56,g72)
    c: Vertical(g71)
    c: Coincident(g72,g53)
    c: Coincident(g52,g71)
    c: Coincident(g58,g68)
    c: Coincident(g73,g60)
    c: Coincident(g61,g73)
    c: Coincident(g74,g63)
    c: Coincident(g64,g74)
    c: Coincident(g66,g75)
    c: Vertical(g74)
    c: Vertical(g75)
    c: PointOnObject(g58,g73)
    c: Vertical(g73)
    c: PointOnObject(g61,g74)
    c: PointOnObject(g64,g75)
    c: Equal(g58,g61)
    c: Equal(g61,g64)
    c: Equal(g59,g62)
    c: Equal(g62,g65)
    c: Equal(g52,g55)
    c: Equal(g54,g57)
    c: Equal(g71,g70)
    c: Equal(g68,g73)
    c: Equal(g73,g74)
    c: Equal(g74,g75)
    c: DistanceY(g71,g71) = 0.35
    c: DistanceY(g54,g54) = 0.32
    c: PointOnObject(g52,g72)
    c: DistanceX(g52,g52) = 0.45
    c: DistanceX(g53,g44) = 0.7
    c: DistanceY(g72,g72) = 1.6
    c: PointOnObject(g52,g44)
    c: DistanceX(g67,g67) = 2.44
    c: DistanceX(g58,g58) = 0.78
    c: DistanceY(g59,g59) = 0.36
FEATURE [Sketcher::SketchObject] Sketch025
  ArcFitTolerance = 1e-06
  AttachmentSupport = -> [XZ_Plane008]
  ExternalTypes = [0]
  FullyConstrained = true
  MakeInternals = false
  MapMode = 5
  Placement = pos=(0,0,0) rot=(1,0,0;1.5708rad)
  _ExternalGeoVersion = 0
  sketch-geometry (15):
    g0: LineSegment StartX=0 StartY=0 StartZ=0 EndX=-15.75 EndY=0 EndZ=0
    g1: LineSegment StartX=-15.75 StartY=0 StartZ=0 EndX=-15.75 EndY=-21.11 EndZ=0
    g2: LineSegment StartX=-15.75 StartY=-21.11 StartZ=0 EndX=0 EndY=-21.11 EndZ=0
    g3: LineSegment StartX=0 StartY=-21.11 StartZ=0 EndX=0 EndY=0 EndZ=0
    g4: Circle CenterX=-2.775 CenterY=-2.775 CenterZ=0 NormalX=0 NormalY=0 NormalZ=1 AngleXU=0 Radius=1.56
    g5: Circle CenterX=-2.775 CenterY=-18.335 CenterZ=0 NormalX=0 NormalY=0 NormalZ=1 AngleXU=0 Radius=1.56
    g6: Circle CenterX=-14.19 CenterY=-2.39 CenterZ=0 NormalX=0 NormalY=0 NormalZ=1 AngleXU=0 Radius=1.05
    g7: Circle CenterX=-14.19 CenterY=-4.73 CenterZ=0 NormalX=0 NormalY=0 NormalZ=1 AngleXU=0 Radius=1.05
    g8: Circle CenterX=-14.19 CenterY=-7.07 CenterZ=0 NormalX=0 NormalY=0 NormalZ=1 AngleXU=0 Radius=1.05
    g9: Circle CenterX=-14.19 CenterY=-9.41 CenterZ=0 NormalX=0 NormalY=0 NormalZ=1 AngleXU=0 Radius=1.05
    g10: Circle CenterX=-14.19 CenterY=-11.75 CenterZ=0 NormalX=0 NormalY=0 NormalZ=1 AngleXU=0 Radius=1.05
    g11: Circle CenterX=-14.19 CenterY=-14.09 CenterZ=0 NormalX=0 NormalY=0 NormalZ=1 AngleXU=0 Radius=1.05
    g12: Circle CenterX=-14.19 CenterY=-16.43 CenterZ=0 NormalX=0 NormalY=0 NormalZ=1 AngleXU=0 Radius=1.05
    g13: Circle CenterX=-14.19 CenterY=-18.77 CenterZ=0 NormalX=0 NormalY=0 NormalZ=1 AngleXU=0 Radius=1.05
    g14: LineSegment [constr] StartX=-14.19 StartY=0 StartZ=0 EndX=-14.19 EndY=-21.11 EndZ=0
  constraints (45):
    c: Coincident(g0,g1)
    c: Coincident(g1,g2)
    c: Coincident(g2,g3)
    c: Coincident(g3,g0)
    c: Horizontal(g0)
    c: Horizontal(g2)
    c: Vertical(g1)
    c: Vertical(g3)
    c: Coincident(g0,g-1)
    c: DistanceX(g2,g2) = 15.75
    c: DistanceY(g1,g1) = 21.11
    c: Equal(g5,g4)
    c: DistanceY(g5,g4) = 15.56
    c: Diameter(g4) = 3.12
    c: DistanceY(g4,g0) = 2.775
    c: DistanceX(g4,g0) = 2.775
    c: DistanceX(g5,g2) = 2.775
    c: Diameter(g6) = 2.1
    c: Equal(g6,g7)
    c: Equal(g7,g8)
    c: Equal(g8,g9)
    c: Equal(g9,g10)
    c: Equal(g10,g11)
    c: Equal(g11,g12)
    c: Equal(g12,g13)
    c: PointOnObject(g14,g0)
    c: PointOnObject(g14,g2)
    c: Vertical(g14)
    c: DistanceX(g0,g14) = 1.56
    c: PointOnObject(g6,g14)
    c: PointOnObject(g7,g14)
    c: PointOnObject(g8,g14)
    c: PointOnObject(g9,g14)
    c: PointOnObject(g10,g14)
    c: PointOnObject(g12,g14)
    c: PointOnObject(g11,g14)
    c: PointOnObject(g13,g14)
    c: DistanceY(g7,g6) = 2.34
    c: DistanceY(g8,g7) = 2.34
    c: DistanceY(g9,g8) = 2.34
    c: DistanceY(g10,g9) = 2.34
    c: DistanceY(g11,g10) = 2.34
    c: DistanceY(g12,g11) = 2.34
    c: DistanceY(g13,g12) = 2.34
    c: DistanceY(g6,g0) = 2.39
FEATURE [PartDesign::Pad] Pad014  label="Pad_Plate"
  Direction = (0,-1,2e-16)
  Length = 1
  Length2 = 10
  Placement = pos=(0,0,0) rot=(1,0,0;1.5708rad)
  Profile = -> Sketch025
  ReferenceAxis = -> Sketch025 [N_Axis]
  Refine = true
  SideType = 0
  Suppressed = false
  Type = 0
  Type2 = 0
FEATURE [PartDesign::Pad] Pad015  label="Pad_Circuit1"
  BaseFeature = -> Pad014
  Direction = (0,-1,2e-16)
  Length = 0.5
  Length2 = 10
  Placement = pos=(0,0,0) rot=(1,0,0;1.5708rad)
  Profile = -> Sketch024
  ReferenceAxis = -> Sketch024 [N_Axis]
  Refine = true
  Reversed = true
  SideType = 0
  Suppressed = false
  Type = 0
  Type2 = 0
FEATURE [Sketcher::SketchObject] Sketch026
  ArcFitTolerance = 1e-06
  AttachmentOffset = pos=(0,0,-0.5) rot=(0,0,1;0rad)
  AttachmentSupport = -> [XZ_Plane008]
  ExternalGeometry = -> [Pad015]
  ExternalTypes = [0]
  FullyConstrained = true
  MakeInternals = false
  MapMode = 5
  Placement = pos=(0,0.5,-1e-16) rot=(1,0,0;1.5708rad)
  _ExternalGeoVersion = 0
  sketch-geometry (56):
    g0: LineSegment StartX=-9.44 StartY=-2.15 StartZ=0 EndX=-10.44 EndY=-2.15 EndZ=0
    g1: LineSegment StartX=-10.44 StartY=-2.15 StartZ=0 EndX=-10.44 EndY=-3.15 EndZ=0
    g2: LineSegment StartX=-10.44 StartY=-3.15 StartZ=0 EndX=-9.44 EndY=-3.15 EndZ=0
    g3: LineSegment StartX=-9.44 StartY=-3.15 StartZ=0 EndX=-9.44 EndY=-2.15 EndZ=0
    g4: LineSegment StartX=-5.84 StartY=-3.65 StartZ=0 EndX=-6.84 EndY=-3.65 EndZ=0
    g5: LineSegment StartX=-6.84 StartY=-3.65 StartZ=0 EndX=-6.84 EndY=-4.65 EndZ=0
    g6: LineSegment StartX=-6.84 StartY=-4.65 StartZ=0 EndX=-5.84 EndY=-4.65 EndZ=0
    g7: LineSegment StartX=-5.84 StartY=-4.65 StartZ=0 EndX=-5.84 EndY=-3.65 EndZ=0
    g8: LineSegment StartX=-9.44 StartY=-3.65 StartZ=0 EndX=-10.44 EndY=-3.65 EndZ=0
    g9: LineSegment StartX=-10.44 StartY=-3.65 StartZ=0 EndX=-10.44 EndY=-4.65 EndZ=0
    g10: LineSegment StartX=-10.44 StartY=-4.65 StartZ=0 EndX=-9.44 EndY=-4.65 EndZ=0
    g11: LineSegment StartX=-9.44 StartY=-4.65 StartZ=0 EndX=-9.44 EndY=-3.65 EndZ=0
    g12: LineSegment StartX=-9.44 StartY=-5.15 StartZ=0 EndX=-10.44 EndY=-5.15 EndZ=0
    g13: LineSegment StartX=-10.44 StartY=-5.15 StartZ=0 EndX=-10.44 EndY=-6.15 EndZ=0
    g14: LineSegment StartX=-10.44 StartY=-6.15 StartZ=0 EndX=-9.44 EndY=-6.15 EndZ=0
    g15: LineSegment StartX=-9.44 StartY=-6.15 StartZ=0 EndX=-9.44 EndY=-5.15 EndZ=0
    g16: LineSegment StartX=-5.84 StartY=-5.15 StartZ=0 EndX=-6.84 EndY=-5.15 EndZ=0
    g17: LineSegment StartX=-6.84 StartY=-5.15 StartZ=0 EndX=-6.84 EndY=-6.15 EndZ=0
    g18: LineSegment StartX=-6.84 StartY=-6.15 StartZ=0 EndX=-5.84 EndY=-6.15 EndZ=0
    g19: LineSegment StartX=-5.84 StartY=-6.15 StartZ=0 EndX=-5.84 EndY=-5.15 EndZ=0
    g20: LineSegment StartX=-1.68 StartY=-9.96 StartZ=0 EndX=-3.06 EndY=-9.96 EndZ=0
    g21: LineSegment StartX=-3.06 StartY=-9.96 StartZ=0 EndX=-3.06 EndY=-12.74 EndZ=0
    g22: LineSegment StartX=-3.06 StartY=-12.74 StartZ=0 EndX=-1.68 EndY=-12.74 EndZ=0
    g23: LineSegment StartX=-1.68 StartY=-12.74 StartZ=0 EndX=-1.68 EndY=-9.96 EndZ=0
    g24: LineSegment StartX=-4.82 StartY=-7.44 StartZ=0 EndX=-10.9 EndY=-7.44 EndZ=0
    g25: LineSegment StartX=-10.9 StartY=-7.44 StartZ=0 EndX=-10.9 EndY=-13.5 EndZ=0
    g26: LineSegment StartX=-10.9 StartY=-13.5 StartZ=0 EndX=-4.82 EndY=-13.5 EndZ=0
    g27: LineSegment StartX=-4.82 StartY=-13.5 StartZ=0 EndX=-4.82 EndY=-7.44 EndZ=0
    g28: LineSegment StartX=-4.8 StartY=-15.5 StartZ=0 EndX=-6.6 EndY=-15.5 EndZ=0
    g29: LineSegment StartX=-6.6 StartY=-15.5 StartZ=0 EndX=-6.6 EndY=-15.96 EndZ=0
    g30: LineSegment StartX=-6.6 StartY=-15.96 StartZ=0 EndX=-4.8 EndY=-15.96 EndZ=0
    g31: LineSegment StartX=-4.8 StartY=-15.96 StartZ=0 EndX=-4.8 EndY=-15.5 EndZ=0
    g32: LineSegment StartX=-4.8 StartY=-16.11 StartZ=0 EndX=-6.6 EndY=-16.11 EndZ=0
    g33: LineSegment StartX=-6.6 StartY=-16.11 StartZ=0 EndX=-6.6 EndY=-16.81 EndZ=0
    g34: LineSegment StartX=-6.6 StartY=-16.81 StartZ=0 EndX=-4.8 EndY=-16.81 EndZ=0
    g35: LineSegment StartX=-4.8 StartY=-16.81 StartZ=0 EndX=-4.8 EndY=-16.11 EndZ=0
    g36: LineSegment StartX=-9.5 StartY=-15.5 StartZ=0 EndX=-11.7 EndY=-15.5 EndZ=0
    g37: LineSegment StartX=-11.7 StartY=-15.5 StartZ=0 EndX=-11.7 EndY=-15.96 EndZ=0
    g38: LineSegment StartX=-11.7 StartY=-15.96 StartZ=0 EndX=-9.5 EndY=-15.96 EndZ=0
    g39: LineSegment StartX=-9.5 StartY=-15.96 StartZ=0 EndX=-9.5 EndY=-15.5 EndZ=0
    g40: LineSegment StartX=-9.5 StartY=-16.11 StartZ=0 EndX=-11.7 EndY=-16.11 EndZ=0
    g41: LineSegment StartX=-11.7 StartY=-16.11 StartZ=0 EndX=-11.7 EndY=-16.81 EndZ=0
    g42: LineSegment StartX=-11.7 StartY=-16.81 StartZ=0 EndX=-9.5 EndY=-16.81 EndZ=0
    g43: LineSegment StartX=-9.5 StartY=-16.81 StartZ=0 EndX=-9.5 EndY=-16.11 EndZ=0
    g44: LineSegment StartX=-4.78 StartY=-18.4 StartZ=0 EndX=-5.58 EndY=-18.4 EndZ=0
    g45: LineSegment StartX=-5.58 StartY=-18.4 StartZ=0 EndX=-5.58 EndY=-19.5 EndZ=0
    g46: LineSegment StartX=-5.58 StartY=-19.5 StartZ=0 EndX=-4.78 EndY=-19.5 EndZ=0
    g47: LineSegment StartX=-4.78 StartY=-19.5 StartZ=0 EndX=-4.78 EndY=-18.4 EndZ=0
    g48: LineSegment StartX=-6.98 StartY=-17.7 StartZ=0 EndX=-8.92 EndY=-17.7 EndZ=0
    g49: LineSegment StartX=-8.92 StartY=-17.7 StartZ=0 EndX=-8.92 EndY=-20.14 EndZ=0
    g50: LineSegment StartX=-8.92 StartY=-20.14 StartZ=0 EndX=-6.98 EndY=-20.14 EndZ=0
    g51: LineSegment StartX=-6.98 StartY=-20.14 StartZ=0 EndX=-6.98 EndY=-17.7 EndZ=0
    g52: LineSegment StartX=-10.88 StartY=-18.4 StartZ=0 EndX=-11.68 EndY=-18.4 EndZ=0
    g53: LineSegment StartX=-11.68 StartY=-18.4 StartZ=0 EndX=-11.68 EndY=-19.5 EndZ=0
    g54: LineSegment StartX=-11.68 StartY=-19.5 StartZ=0 EndX=-10.88 EndY=-19.5 EndZ=0
    g55: LineSegment StartX=-10.88 StartY=-19.5 StartZ=0 EndX=-10.88 EndY=-18.4 EndZ=0
  constraints (168):
    c: Coincident(g0,g1)
    c: Coincident(g1,g2)
    c: Coincident(g2,g3)
    c: Coincident(g3,g0)
    c: Horizontal(g0)
    c: Horizontal(g2)
    c: Vertical(g1)
    c: Vertical(g3)
    c: Coincident(g4,g5)
    c: Coincident(g5,g6)
    c: Coincident(g6,g7)
    c: Coincident(g7,g4)
    c: Horizontal(g4)
    c: Horizontal(g6)
    c: Vertical(g5)
    c: Vertical(g7)
    c: Coincident(g8,g9)
    c: Coincident(g9,g10)
    c: Coincident(g10,g11)
    c: Coincident(g11,g8)
    c: Horizontal(g8)
    c: Horizontal(g10)
    c: Vertical(g9)
    c: Vertical(g11)
    c: Coincident(g12,g13)
    c: Coincident(g13,g14)
    c: Coincident(g14,g15)
    c: Coincident(g15,g12)
    c: Horizontal(g12)
    c: Horizontal(g14)
    c: Vertical(g13)
    c: Vertical(g15)
    c: Coincident(g16,g17)
    c: Coincident(g17,g18)
    c: Coincident(g18,g19)
    c: Coincident(g19,g16)
    c: Horizontal(g16)
    c: Horizontal(g18)
    c: Vertical(g17)
    c: Vertical(g19)
    c: Coincident(g20,g21)
    c: Coincident(g21,g22)
    c: Coincident(g22,g23)
    c: Coincident(g23,g20)
    c: Horizontal(g20)
    c: Horizontal(g22)
    c: Vertical(g21)
    c: Vertical(g23)
    c: Coincident(g24,g25)
    c: Coincident(g25,g26)
    c: Coincident(g26,g27)
    c: Coincident(g27,g24)
    c: Horizontal(g24)
    c: Horizontal(g26)
    c: Vertical(g25)
    c: Vertical(g27)
    c: Coincident(g28,g29)
    c: Coincident(g29,g30)
    c: Coincident(g30,g31)
    c: Coincident(g31,g28)
    c: Horizontal(g28)
    c: Horizontal(g30)
    c: Vertical(g29)
    c: Vertical(g31)
    c: Coincident(g32,g33)
    c: Coincident(g33,g34)
    c: Coincident(g34,g35)
    c: Coincident(g35,g32)
    c: Horizontal(g32)
    c: Horizontal(g34)
    c: Vertical(g33)
    c: Vertical(g35)
    c: Coincident(g36,g37)
    c: Coincident(g37,g38)
    c: Coincident(g38,g39)
    c: Coincident(g39,g36)
    c: Horizontal(g36)
    c: Horizontal(g38)
    c: Vertical(g37)
    c: Vertical(g39)
    c: Coincident(g40,g41)
    c: Coincident(g41,g42)
    c: Coincident(g42,g43)
    c: Coincident(g43,g40)
    c: Horizontal(g40)
    c: Horizontal(g42)
    c: Vertical(g41)
    c: Vertical(g43)
    c: Coincident(g44,g45)
    c: Coincident(g45,g46)
    c: Coincident(g46,g47)
    c: Coincident(g47,g44)
    c: Horizontal(g44)
    c: Horizontal(g46)
    c: Vertical(g45)
    c: Vertical(g47)
    c: Coincident(g48,g49)
    c: Coincident(g49,g50)
    c: Coincident(g50,g51)
    c: Coincident(g51,g48)
    c: Horizontal(g48)
    c: Horizontal(g50)
    c: Vertical(g49)
    c: Vertical(g51)
    c: Coincident(g52,g53)
    c: Coincident(g53,g54)
    c: Coincident(g54,g55)
    c: Coincident(g55,g52)
    c: Horizontal(g52)
    c: Horizontal(g54)
    c: Vertical(g53)
    c: Vertical(g55)
    c: Equal(g0,g3)
    c: Equal(g3,g4)
    c: Equal(g4,g7)
    c: Equal(g7,g16)
    c: Equal(g16,g19)
    c: Equal(g19,g12)
    c: Equal(g12,g15)
    c: Equal(g15,g8)
    c: Equal(g8,g11)
    c: PointOnObject(g0,g-3)
    c: PointOnObject(g2,g-4)
    c: DistanceX(g-4,g1) = 0.6
    c: PointOnObject(g8,g-5)
    c: PointOnObject(g1,g9)
    c: PointOnObject(g12,g-6)
    c: PointOnObject(g9,g13)
    c: PointOnObject(g5,g17)
    c: PointOnObject(g4,g8)
    c: PointOnObject(g16,g12)
    c: DistanceX(g-7,g4) = 0.6
    c: DistanceX(g-8,g24) = 0.64
    c: DistanceY(g24,g-8) = 0.64
    c: DistanceX(g26,g-9) = 0.64
    c: DistanceY(g-9,g26) = 0.64
    c: PointOnObject(g20,g-11)
    c: PointOnObject(g20,g-10)
    c: DistanceY(g20,g-10) = 0.8
    c: DistanceY(g-10,g21) = 0.8
    c: DistanceX(g50,g-25) = 0.25
    c: DistanceY(g-25,g50) = 0.25
    c: DistanceY(g48,g-24) = 0.25
    c: DistanceX(g-24,g48) = 0.25
    c: PointOnObject(g28,g-12)
    c: PointOnObject(g29,g-13)
    c: DistanceX(g-12,g28) = 0.8
    c: DistanceX(g28,g-12) = 0.8
    c: PointOnObject(g32,g-14)
    c: PointOnObject(g33,g-15)
    c: PointOnObject(g29,g33)
    c: PointOnObject(g30,g35)
    c: PointOnObject(g36,g-16)
    c: PointOnObject(g37,g-17)
    c: DistanceX(g-16,g36) = 0.6
    c: DistanceX(g36,g-16) = 0.6
    c: PointOnObject(g40,g-18)
    c: PointOnObject(g41,g-19)
    c: PointOnObject(g37,g41)
    c: PointOnObject(g38,g43)
    c: PointOnObject(g52,g-23)
    c: PointOnObject(g54,g-22)
    c: DistanceY(g52,g-22) = 0.6
    c: DistanceY(g-23,g53) = 0.6
    c: PointOnObject(g44,g-20)
    c: PointOnObject(g46,g-21)
    c: PointOnObject(g44,g52)
    c: PointOnObject(g45,g54)
FEATURE [PartDesign::Pad] Pad016  label="Pad_Circuit2"
  BaseFeature = -> Pad015
  Direction = (0,-1,2e-16)
  Length = 1
  Length2 = 10
  Placement = pos=(0,0,0) rot=(1,0,0;1.5708rad)
  Profile = -> Sketch026
  ReferenceAxis = -> Sketch026 [N_Axis]
  Refine = true
  SideType = 2
  Suppressed = false
  Type = 0
  Type2 = 0
FEATURE [PartDesign::CoordinateSystem] MPU6050
  AttacherType = Attacher::AttachEngine3D
  AttachmentOffset = pos=(0,0,0) rot=(-0.57735,0.57735,-0.57735;2.0944rad)
  AttachmentSupport = -> [Pad016]
  MapMode = 11
  Placement = pos=(-2.775,0,-2.775) rot=(0,0,1;0rad)
FEATURE [PartDesign::Body] Body006  label="Body_MPU6050"
  AllowCompound = false
  Group = -> [Sketch025,Pad014,Sketch024,Pad015,Sketch026,Pad016,MPU6050]
  Origin = -> Origin008
  Tip = -> Pad016
COMPONENT P6 — recipe-attached ("Body_BearingLock", modeled in this document).
Construction recipe (the document's own serialized feature program — sketch geometry with constraints, then the solid features built on it; lengths are millimeters unless a unit is written):

FEATURE [Sketcher::SketchObject] Sketch030
  ArcFitTolerance = 1e-06
  AttachmentSupport = -> [XY_Plane009]
  ExternalTypes = [0]
  FullyConstrained = true
  MakeInternals = false
  MapMode = 5
  _ExternalGeoVersion = 0
  sketch-geometry (6):
    g0: ArcOfCircle CenterX=0 CenterY=-84.8494 CenterZ=0 NormalX=0 NormalY=0 NormalZ=1 AngleXU=0 Radius=25 StartAngle=2.3746 EndAngle=7.05018
    g1: LineSegment StartX=18 StartY=-67.5 StartZ=0 EndX=-18 EndY=-67.5 EndZ=0
    g2: Circle CenterX=15.1 CenterY=-75.5 CenterZ=0 NormalX=0 NormalY=0 NormalZ=1 AngleXU=0 Radius=1.8
    g3: Circle CenterX=-15.1 CenterY=-75.5 CenterZ=0 NormalX=0 NormalY=0 NormalZ=1 AngleXU=0 Radius=1.8
    g4: Circle CenterX=0 CenterY=-105.5 CenterZ=0 NormalX=0 NormalY=0 NormalZ=1 AngleXU=0 Radius=1.8
    g5: Circle CenterX=0 CenterY=-84.8494 CenterZ=0 NormalX=0 NormalY=0 NormalZ=1 AngleXU=0 Radius=9
  constraints (17):
    c: PointOnObject(g0,g-2)
    c: Diameter(g0) = 50
    c: Horizontal(g1)
    c: Coincident(g0,g1)
    c: Coincident(g0,g1)
    c: DistanceX(g1,g1) = 36
    c: PointOnObject(g4,g-2)
    c: Equal(g3,g2)
    c: Equal(g2,g4)
    c: Diameter(g2) = 3.6
    c: Symmetric(g2,g3,g-2)
    c: DistanceX(g3,g2) = 30.2
    c: DistanceY(g2,g0) = 8
    c: DistanceY(g4,g2) = 30
    c: DistanceY(g0,g-1) = 67.5
    c: Coincident(g5,g0)
    c: Diameter(g5) = 18
FEATURE [PartDesign::Pad] Pad018
  Direction = (0,0,1)
  Length = 3
  Length2 = 10
  Profile = -> Sketch030
  ReferenceAxis = -> Sketch030 [N_Axis]
  Refine = true
  Reversed = true
  SideType = 0
  Suppressed = false
  Type = 0
  Type2 = 0
FEATURE [PartDesign::CoordinateSystem] BearingLock
  AttacherType = Attacher::AttachEngine3D
  AttachmentOffset = pos=(0,0,0) rot=(0,0,-1;1.5708rad)
  AttachmentSupport = -> [Pad018]
  MapMode = 11
  Placement = pos=(0,-84.8494,-3) rot=(0,0,1;0rad)
FEATURE [Sketcher::SketchObject] Sketch031
  ArcFitTolerance = 1e-06
  AttachmentSupport = -> [Pad018]
  ExternalGeometry = -> [Pad018]
  ExternalTypes = [0]
  FullyConstrained = true
  MakeInternals = false
  MapMode = 5
  Placement = pos=(0,0,-3) rot=(1,0,0;3.14159rad)
  _ExternalGeoVersion = 0
  sketch-geometry (2):
    g0: Circle CenterX=-15 CenterY=83.5 CenterZ=0 NormalX=0 NormalY=0 NormalZ=1 AngleXU=0 Radius=4
    g1: Circle CenterX=15 CenterY=83.5 CenterZ=0 NormalX=0 NormalY=0 NormalZ=1 AngleXU=0 Radius=4
  constraints (5):
    c: Equal(g0,g1)
    c: Diameter(g0) = 8
    c: Symmetric(g0,g1,g-2)
    c: DistanceX(g0,g1) = 30
    c: DistanceY(g-3,g0) = 8
FEATURE [PartDesign::Pad] Pad019
  BaseFeature = -> Pad018
  Direction = (0,0,-1)
  Length = 20
  Length2 = 10
  Profile = -> Sketch031
  ReferenceAxis = -> Sketch031 [N_Axis]
  Refine = true
  SideType = 0
  Suppressed = false
  Type = 0
  Type2 = 0
FEATURE [PartDesign::Fillet] Fillet
  Base = -> Pad019 [Edge24,Edge22]
  BaseFeature = -> Pad019
  Radius = 3.5
  Refine = true
  SupportTransform = false
  Suppressed = false
  UseAllEdges = false
FEATURE [PartDesign::Body] Body007  label="Body_BearingLock"
  AllowCompound = false
  Group = -> [Sketch030,Pad018,BearingLock,Sketch031,Pad019,Fillet]
  Origin = -> Origin009
  Tip = -> Fillet
COMPONENT P7 — recipe-attached ("Body_Battery_Tattu", modeled in this document).
Construction recipe (the document's own serialized feature program — sketch geometry with constraints, then the solid features built on it; lengths are millimeters unless a unit is written):

FEATURE [Sketcher::SketchObject] Sketch048
  ArcFitTolerance = 1e-06
  AttachmentSupport = -> [XZ_Plane110]
  ExternalTypes = [0]
  FullyConstrained = true
  MakeInternals = false
  MapMode = 5
  Placement = pos=(0,0,0) rot=(1,0,0;1.5708rad)
  _ExternalGeoVersion = 0
  sketch-geometry (6):
    g0: Circle CenterX=8.5 CenterY=-6.5 CenterZ=0 NormalX=0 NormalY=0 NormalZ=1 AngleXU=0 Radius=1.5
    g1: Circle CenterX=-8.5 CenterY=-6.5 CenterZ=0 NormalX=0 NormalY=0 NormalZ=1 AngleXU=0 Radius=1.5
    g2: Circle CenterX=-5.3 CenterY=-6.5 CenterZ=0 NormalX=0 NormalY=0 NormalZ=1 AngleXU=0 Radius=0.8
    g3: Circle CenterX=-2.8 CenterY=-6.5 CenterZ=0 NormalX=0 NormalY=0 NormalZ=1 AngleXU=0 Radius=0.8
    g4: Circle CenterX=2.8 CenterY=-6.5 CenterZ=0 NormalX=0 NormalY=0 NormalZ=1 AngleXU=0 Radius=0.8
    g5: Circle CenterX=5.3 CenterY=-6.5 CenterZ=0 NormalX=0 NormalY=0 NormalZ=1 AngleXU=0 Radius=0.8
  constraints (15):
    c: Equal(g0,g1)
    c: Equal(g5,g4)
    c: Equal(g4,g3)
    c: Equal(g3,g2)
    c: Symmetric(g0,g1,g-2)
    c: Diameter(g0) = 3
    c: DistanceX(g1,g0) = 17
    c: DistanceY(g0,g-1) = 6.5
    c: Diameter(g2) = 1.6
    c: Symmetric(g5,g2,g-2)
    c: Symmetric(g4,g3,g-2)
    c: DistanceX(g3,g4) = 5.6
    c: DistanceX(g2,g5) = 10.6
    c: DistanceY(g5,g-1) = 6.5
    c: DistanceY(g4,g-1) = 6.5
FEATURE [Sketcher::SketchObject] Sketch049
  ArcFitTolerance = 1e-06
  AttachmentSupport = -> [XZ_Plane110]
  ExternalTypes = [0]
  FullyConstrained = true
  MakeInternals = false
  MapMode = 5
  Placement = pos=(0,0,0) rot=(1,0,0;1.5708rad)
  _ExternalGeoVersion = 0
  sketch-geometry (4):
    g0: LineSegment StartX=-10 StartY=8 StartZ=0 EndX=-10 EndY=-8 EndZ=0
    g1: LineSegment StartX=-10 StartY=-8 StartZ=0 EndX=10 EndY=-8 EndZ=0
    g2: LineSegment StartX=10 StartY=-8 StartZ=0 EndX=10 EndY=8 EndZ=0
    g3: LineSegment StartX=10 StartY=8 StartZ=0 EndX=-10 EndY=8 EndZ=0
  constraints (11):
    c: Coincident(g0,g1)
    c: Coincident(g1,g2)
    c: Coincident(g2,g3)
    c: Coincident(g3,g0)
    c: Vertical(g0)
    c: Vertical(g2)
    c: Horizontal(g1)
    c: Horizontal(g3)
    c: Symmetric(g1,g0,g-1)
    c: DistanceY(g0,g0) = 16
    c: DistanceX(g1,g1) = 20
FEATURE [PartDesign::Pad] Pad030
  Direction = (0,-1,2e-16)
  Length = 64.5
  Length2 = 10
  Placement = pos=(0,0,0) rot=(1,0,0;1.5708rad)
  Profile = -> Sketch049
  ReferenceAxis = -> Sketch049 [N_Axis]
  Refine = true
  SideType = 0
  Suppressed = false
  Type = 0
  Type2 = 0
FEATURE [PartDesign::Fillet] Fillet007
  Base = -> Pad030 [Edge10,Edge4]
  BaseFeature = -> Pad030
  Placement = pos=(0,0,0) rot=(1,0,0;1.5708rad)
  Radius = 3
  Refine = true
  SupportTransform = false
  Suppressed = false
  UseAllEdges = false
FEATURE [PartDesign::Fillet] Fillet008
  Base = -> Fillet007 [Edge3,Edge13]
  BaseFeature = -> Fillet007
  Placement = pos=(0,0,0) rot=(1,0,0;1.5708rad)
  Radius = 9
  Refine = true
  SupportTransform = false
  Suppressed = false
  UseAllEdges = false
FEATURE [PartDesign::Pad] Pad031  label="Pad_Battery"
  BaseFeature = -> Fillet008
  Direction = (0,-1,2e-16)
  Length = 10
  Length2 = 10
  Placement = pos=(0,0,0) rot=(1,0,0;1.5708rad)
  Profile = -> Sketch048
  ReferenceAxis = -> Sketch048 [N_Axis]
  Refine = true
  SideType = 2
  Suppressed = false
  Type = 0
  Type2 = 0
FEATURE [PartDesign::CoordinateSystem] Battery
  AttacherType = Attacher::AttachEngine3D
  AttachmentSupport = -> [Pad031]
  MapMode = 45
  Placement = pos=(-7,-64.5,2.89e-14) rot=(0,0,1;0rad)
FEATURE [PartDesign::Body] Body014  label="Body_Battery_Tattu"
  AllowCompound = false
  Group = -> [Sketch049,Pad030,Fillet007,Fillet008,Sketch048,Pad031,Battery]
  Origin = -> Origin110
  Tip = -> Pad031
COMPONENT P8 — recipe-attached ("Body_Trepied", modeled in this document).
Construction recipe (the document's own serialized feature program — sketch geometry with constraints, then the solid features built on it; lengths are millimeters unless a unit is written):

FEATURE [Sketcher::SketchObject] Sketch051
  ArcFitTolerance = 1e-06
  AttachmentSupport = -> [XY_Plane111]
  ExternalTypes = [0]
  FullyConstrained = true
  MakeInternals = false
  MapMode = 5
  _ExternalGeoVersion = 0
  sketch-geometry (1):
    g0: Circle CenterX=0 CenterY=55 CenterZ=0 NormalX=0 NormalY=0 NormalZ=1 AngleXU=0 Radius=2.3
  constraints (3):
    c: PointOnObject(g0,g-2)
    c: DistanceY(g-1,g0) = 55
    c: Diameter(g0) = 4.6
FEATURE [Sketcher::SketchObject] Sketch052
  ArcFitTolerance = 1e-06
  AttachmentSupport = -> [XY_Plane111]
  ExternalTypes = [0]
  FullyConstrained = true
  MakeInternals = false
  MapMode = 5
  _ExternalGeoVersion = 0
  sketch-geometry (1):
    g0: Circle CenterX=0 CenterY=0 CenterZ=0 NormalX=0 NormalY=0 NormalZ=1 AngleXU=0 Radius=62.5
  constraints (2):
    c: Coincident(g0,g-1)
    c: Diameter(g0) = 125
FEATURE [PartDesign::Pad] Pad032
  Direction = (0,0,1)
  Length = 3
  Length2 = 10
  Profile = -> Sketch052
  ReferenceAxis = -> Sketch052 [N_Axis]
  Refine = true
  SideType = 0
  Suppressed = false
  Type = 0
  Type2 = 0
FEATURE [PartDesign::Fillet] Fillet009
  Base = -> Pad032 [Edge3,Edge2]
  BaseFeature = -> Pad032
  Radius = 1.49
  Refine = true
  SupportTransform = false
  Suppressed = false
  UseAllEdges = false
FEATURE [PartDesign::Pocket] Pocket016
  BaseFeature = -> Fillet009
  Direction = (0,0,-1)
  Length = 5
  Length2 = 5
  Profile = -> Sketch051
  ReferenceAxis = -> Sketch051 [N_Axis]
  Refine = true
  Reversed = true
  SideType = 0
  Suppressed = false
  Type = 0
  Type2 = 0
FEATURE [PartDesign::PolarPattern] PolarPattern006
  Angle = 360
  Axis = -> Sketch051 [N_Axis]
  BaseFeature = -> Pocket016
  Mode = 0
  Occurrences = 6
  Offset = 120
  Originals = -> [Pocket016]
  Refine = true
  SpacingPattern = [0]
  Spacings = [-1,-1,-1,-1,-1]
  Suppressed = false
  TransformMode = 0
FEATURE [PartDesign::CoordinateSystem] Trepied
  AttacherType = Attacher::AttachEngine3D
  AttachmentOffset = pos=(0,0,0) rot=(0.707107,0.707107,0;3.14159rad)
  AttachmentSupport = -> [PolarPattern006]
  MapMode = 11
  Placement = pos=(-6.7e-15,-55,3) rot=(0,0,1;0rad)
FEATURE [Sketcher::SketchObject] Sketch053
  ArcFitTolerance = 1e-06
  AttachmentSupport = -> [PolarPattern006]
  ExternalTypes = [0]
  FullyConstrained = true
  MakeInternals = false
  MapMode = 5
  Placement = pos=(0,0,3) rot=(0,0,1;0rad)
  _ExternalGeoVersion = 0
  sketch-geometry (2):
    g0: Circle CenterX=0 CenterY=0 CenterZ=0 NormalX=0 NormalY=0 NormalZ=1 AngleXU=0 Radius=37
    g1: Circle CenterX=0 CenterY=0 CenterZ=0 NormalX=0 NormalY=0 NormalZ=1 AngleXU=0 Radius=35.3
  constraints (4):
    c: Coincident(g0,g-1)
    c: Diameter(g0) = 74
    c: Coincident(g1,g0)
    c: Diameter(g1) = 70.6
FEATURE [PartDesign::Pad] Pad033
  BaseFeature = -> PolarPattern006
  Direction = (0,0,1)
  Length = 60
  Length2 = 10
  Profile = -> Sketch053
  ReferenceAxis = -> Sketch053 [N_Axis]
  Refine = true
  Reversed = true
  SideType = 0
  Suppressed = false
  Type = 0
  Type2 = 0
FEATURE [PartDesign::CoordinateSystem] Trepied_Bottom
  AttacherType = Attacher::AttachEngine3D
  AttachmentOffset = pos=(0,0,0) rot=(0,0,-1;0.523599rad)
  AttachmentSupport = -> [Pad033]
  MapMode = 45
  Placement = pos=(-47.6314,27.5,3) rot=(0,0,1;0.523595rad)
FEATURE [PartDesign::CoordinateSystem] Trepied_Axial
  AttacherType = Attacher::AttachEngine3D
  AttachmentSupport = -> [Pad033]
  MapMode = 45
  Placement = pos=(1.683e-13,3.2e-15,-57) rot=(0,0,1;0rad)
FEATURE [PartDesign::Body] Body015  label="Body_Trepied"
  AllowCompound = false
  Group = -> [Sketch052,Pad032,Fillet009,Sketch051,Pocket016,PolarPattern006,Trepied,Sketch053,Pad033,Trepied_Bottom,Trepied_Axial]
  Origin = -> Origin111
  Tip = -> Pad033
COMPONENT P9 — recipe-attached ("Body_Pedestral", modeled in this document).
Construction recipe (the document's own serialized feature program — sketch geometry with constraints, then the solid features built on it; lengths are millimeters unless a unit is written):

FEATURE [Sketcher::SketchObject] Sketch054
  ArcFitTolerance = 1e-06
  AttachmentSupport = -> [XY_Plane112]
  ExternalTypes = [0]
  FullyConstrained = true
  MakeInternals = false
  MapMode = 5
  _ExternalGeoVersion = 0
  sketch-geometry (1):
    g0: Circle CenterX=0 CenterY=0 CenterZ=0 NormalX=0 NormalY=0 NormalZ=1 AngleXU=0 Radius=30
  constraints (2):
    c: Diameter(g0) = 60
    c: Coincident(g-1,g0)
FEATURE [PartDesign::Pad] Pad034
  Direction = (0,0,1)
  Length = 30
  Length2 = 10
  Profile = -> Sketch054
  ReferenceAxis = -> Sketch054 [N_Axis]
  Refine = true
  SideType = 0
  Suppressed = false
  Type = 0
  Type2 = 0
FEATURE [Sketcher::SketchObject] Sketch055
  ArcFitTolerance = 1e-06
  AttachmentSupport = -> [XZ_Plane112]
  ExternalGeometry = -> [Pad034]
  ExternalTypes = [0]
  FullyConstrained = true
  MakeInternals = false
  MapMode = 5
  Placement = pos=(0,0,0) rot=(1,0,0;1.5708rad)
  _ExternalGeoVersion = 0
  sketch-geometry (8):
    g0: LineSegment StartX=62.9979 StartY=30 StartZ=0 EndX=197.788 EndY=-162.501 EndZ=0
    g1: LineSegment StartX=197.788 StartY=-162.501 StartZ=0 EndX=157.788 EndY=-162.501 EndZ=0
    g2: LineSegment StartX=157.788 StartY=-162.501 StartZ=0 EndX=30 EndY=20 EndZ=0
    g3: LineSegment StartX=-157.788 StartY=-162.501 StartZ=0 EndX=-197.788 EndY=-162.501 EndZ=0
    g4: LineSegment StartX=-197.788 StartY=-162.501 StartZ=0 EndX=-62.9979 EndY=30 EndZ=0
    g5: LineSegment StartX=-62.9979 StartY=30 StartZ=0 EndX=62.9979 EndY=30 EndZ=0
    g6: LineSegment StartX=30 StartY=20 StartZ=0 EndX=-30 EndY=20 EndZ=0
    g7: LineSegment StartX=-30 StartY=20 StartZ=0 EndX=-157.788 EndY=-162.501 EndZ=0
  constraints (21):
    c: Coincident(g0,g1)
    c: Horizontal(g1)
    c: Coincident(g1,g2)
    c: Parallel(g0,g2)
    c: DistanceX(g1,g1) = 40
    c: Distance(g0) = 235
    c: Angle(g-1,g2) = 2.18166
    c: PointOnObject(g2,g-3)
    c: Horizontal(g3)
    c: Coincident(g3,g4)
    c: Coincident(g4,g5)
    c: Coincident(g6,g7)
    c: Coincident(g7,g3)
    c: Symmetric(g3,g1,g-2)
    c: DistanceX(g3,g3) = 40
    c: Symmetric(g4,g0,g-2)
    c: Symmetric(g6,g2,g-2)
    c: Coincident(g5,g0)
    c: Coincident(g6,g2)
    c: DistanceY(g6,g4) = 10
    c: PointOnObject(g-3,g5)
FEATURE [PartDesign::Pad] Pad035
  BaseFeature = -> Pad034
  Direction = (0,-1,2e-16)
  Length = 50
  Length2 = 10
  Profile = -> Sketch055
  ReferenceAxis = -> Sketch055 [N_Axis]
  Refine = true
  SideType = 2
  Suppressed = false
  Type = 0
  Type2 = 0
FEATURE [Sketcher::SketchObject] Sketch056
  ArcFitTolerance = 1e-06
  AttachmentSupport = -> [Pad035]
  ExternalTypes = [0]
  FullyConstrained = true
  MakeInternals = false
  MapMode = 5
  Placement = pos=(0,0,30) rot=(0,0,1;0rad)
  _ExternalGeoVersion = 0
  sketch-geometry (1):
    g0: Circle CenterX=0 CenterY=0 CenterZ=0 NormalX=0 NormalY=0 NormalZ=1 AngleXU=0 Radius=25.3
  constraints (2):
    c: Coincident(g0,g-1)
    c: Diameter(g0) = 50.6
FEATURE [Sketcher::SketchObject] Sketch057
  ArcFitTolerance = 1e-06
  AttachmentOffset = pos=(0,0,0) rot=(0,1,0;2.0944rad)
  AttachmentSupport = -> [XZ_Plane112]
  ExternalTypes = [0]
  FullyConstrained = true
  MakeInternals = false
  MapMode = 5
  Placement = pos=(0,0,0) rot=(0.377964,0.654654,0.654654;2.41886rad)
  _ExternalGeoVersion = 0
  sketch-geometry (6):
    g0: LineSegment StartX=0 StartY=30 StartZ=0 EndX=62.9979 EndY=30 EndZ=0
    g1: LineSegment StartX=62.9979 StartY=30 StartZ=0 EndX=197.788 EndY=-162.501 EndZ=0
    g2: LineSegment StartX=197.788 StartY=-162.501 StartZ=0 EndX=157.788 EndY=-162.501 EndZ=0
    g3: LineSegment StartX=157.788 StartY=-162.501 StartZ=0 EndX=30 EndY=20 EndZ=0
    g4: LineSegment StartX=30 StartY=20 StartZ=0 EndX=0 EndY=20 EndZ=0
    g5: LineSegment StartX=0 StartY=20 StartZ=0 EndX=0 EndY=30 EndZ=0
  constraints (18):
    c: PointOnObject(g0,g-2)
    c: Horizontal(g0)
    c: Coincident(g0,g1)
    c: Coincident(g1,g2)
    c: Horizontal(g2)
    c: Coincident(g2,g3)
    c: Coincident(g3,g4)
    c: Coincident(g4,g5)
    c: Coincident(g5,g0)
    c: Vertical(g5)
    c: Horizontal(g4)
    c: DistanceY(g5,g5) = 10
    c: DistanceX(g2,g2) = 40
    c: Angle(g-1,g3) = 2.18166
    c: Distance(g1) = 235
    c: Parallel(g3,g1)
    c: DistanceY(g-1,g4) = 20
    c: DistanceX(g4,g4) = 30
FEATURE [Sketcher::SketchObject] Sketch058
  ArcFitTolerance = 1e-06
  AttachmentOffset = pos=(0,0,0) rot=(0,1,0;1.0472rad)
  AttachmentSupport = -> [XZ_Plane112]
  ExternalTypes = [0]
  FullyConstrained = true
  MakeInternals = false
  MapMode = 5
  Placement = pos=(0,0,0) rot=(0.774597,0.447214,0.447214;1.82348rad)
  _ExternalGeoVersion = 0
  sketch-geometry (6):
    g0: LineSegment StartX=0 StartY=30 StartZ=0 EndX=62.9979 EndY=30 EndZ=0
    g1: LineSegment StartX=62.9979 StartY=30 StartZ=0 EndX=197.788 EndY=-162.501 EndZ=0
    g2: LineSegment StartX=197.788 StartY=-162.501 StartZ=0 EndX=157.788 EndY=-162.501 EndZ=0
    g3: LineSegment StartX=157.788 StartY=-162.501 StartZ=0 EndX=30 EndY=20 EndZ=0
    g4: LineSegment StartX=30 StartY=20 StartZ=0 EndX=0 EndY=20 EndZ=0
    g5: LineSegment StartX=0 StartY=20 StartZ=0 EndX=0 EndY=30 EndZ=0
  constraints (18):
    c: PointOnObject(g0,g-2)
    c: Horizontal(g0)
    c: Coincident(g0,g1)
    c: Coincident(g1,g2)
    c: Horizontal(g2)
    c: Coincident(g2,g3)
    c: Coincident(g3,g4)
    c: Coincident(g4,g5)
    c: Coincident(g5,g0)
    c: Vertical(g5)
    c: Horizontal(g4)
    c: DistanceY(g5,g5) = 10
    c: DistanceX(g2,g2) = 40
    c: Angle(g-1,g3) = 2.18166
    c: Distance(g1) = 235
    c: Parallel(g3,g1)
    c: DistanceY(g-1,g4) = 20
    c: DistanceX(g4,g4) = 30
FEATURE [Sketcher::SketchObject] Sketch059
  ArcFitTolerance = 1e-06
  AttachmentOffset = pos=(0,0,-163) rot=(0,0,1;0rad)
  AttachmentSupport = -> [XY_Plane112]
  ExternalTypes = [0]
  FullyConstrained = true
  MakeInternals = false
  MapMode = 5
  Placement = pos=(0,0,-163) rot=(0,0,1;0rad)
  _ExternalGeoVersion = 0
  sketch-geometry (6):
    g0: ArcOfCircle CenterX=0 CenterY=0 CenterZ=0 NormalX=0 NormalY=0 NormalZ=1 AngleXU=0 Radius=145 StartAngle=1.8326 EndAngle=3.40339
    g1: ArcOfCircle CenterX=0 CenterY=0 CenterZ=0 NormalX=0 NormalY=0 NormalZ=1 AngleXU=0 Radius=205 StartAngle=1.8326 EndAngle=3.40339
    g2: LineSegment [constr] StartX=0 StartY=0 StartZ=0 EndX=-212.504 EndY=-56.9402 EndZ=0
    g3: LineSegment [constr] StartX=0 StartY=0 StartZ=0 EndX=-56.9402 EndY=212.504 EndZ=0
    g4: ArcOfCircle CenterX=-169.037 CenterY=-45.2933 CenterZ=0 NormalX=0 NormalY=0 NormalZ=1 AngleXU=0 Radius=30 StartAngle=3.40339 EndAngle=6.54498
    g5: ArcOfCircle CenterX=-45.2933 CenterY=169.037 CenterZ=0 NormalX=0 NormalY=0 NormalZ=1 AngleXU=0 Radius=30 StartAngle=4.97419 EndAngle=8.11578
  constraints (20):
    c: Coincident(g0,g-1)
    c: Coincident(g2,g0)
    c: Coincident(g3,g1)
    c: Coincident(g1,g0)
    c: PointOnObject(g0,g2)
    c: PointOnObject(g1,g2)
    c: PointOnObject(g1,g3)
    c: Angle(g2,g-1) = 2.87979
    c: Angle(g-2,g3) = 0.261799
    c: Radius(g0) = 145
    c: Diameter(g5) = 60
    c: Coincident(g5,g1)
    c: Coincident(g5,g0)
    c: Diameter(g4) = 60
    c: Coincident(g4,g1)
    c: Coincident(g4,g0)
    c: PointOnObject(g4,g2)
    c: PointOnObject(g0,g3)
    c: Equal(g3,g2)
    c: Distance(g3) = 220
FEATURE [PartDesign::Pad] Pad036
  BaseFeature = -> Pad035
  Direction = (0,0,1)
  Length = 5
  Length2 = 10
  Profile = -> Sketch059
  ReferenceAxis = -> Sketch059 [N_Axis]
  Refine = true
  SideType = 0
  Suppressed = false
  Type = 0
  Type2 = 0
FEATURE [Sketcher::SketchObject] Sketch004
  ArcFitTolerance = 1e-06
  AttachmentSupport = -> [Pad036]
  ExternalGeometry = -> [Pad036]
  ExternalTypes = [0]
  FullyConstrained = true
  MakeInternals = false
  MapMode = 5
  Placement = pos=(0,0,-158) rot=(0,0,1;0rad)
  _ExternalGeoVersion = 0
  sketch-geometry (4):
    g0: ArcOfCircle CenterX=0 CenterY=0 CenterZ=0 NormalX=0 NormalY=0 NormalZ=1 AngleXU=0 Radius=145 StartAngle=6.02139 EndAngle=7.59218
    g1: ArcOfCircle CenterX=0 CenterY=0 CenterZ=0 NormalX=0 NormalY=0 NormalZ=1 AngleXU=0 Radius=205 StartAngle=6.02139 EndAngle=7.59218
    g2: ArcOfCircle CenterX=45.2933 CenterY=169.037 CenterZ=0 NormalX=0 NormalY=0 NormalZ=1 AngleXU=0 Radius=30 StartAngle=1.309 EndAngle=4.45059
    g3: ArcOfCircle CenterX=169.037 CenterY=-45.2933 CenterZ=0 NormalX=0 NormalY=0 NormalZ=1 AngleXU=0 Radius=30 StartAngle=2.87979 EndAngle=6.02139
  constraints (11):
    c: Coincident(g0,g-1)
    c: Coincident(g1,g0)
    c: Symmetric(g-3,g0,g-2)
    c: Symmetric(g1,g-3,g-2)
    c: Coincident(g2,g1)
    c: Coincident(g2,g0)
    c: Coincident(g3,g1)
    c: Coincident(g3,g0)
    c: Radius(g2) = 30
    c: Radius(g3) = 30
    c: Symmetric(g-4,g3,g-2)
FEATURE [PartDesign::Pad] Pad003
  BaseFeature = -> Pad036
  Direction = (0,0,1)
  Length = 5
  Length2 = 10
  Profile = -> Sketch004
  ReferenceAxis = -> Sketch004 [N_Axis]
  Refine = true
  Reversed = true
  SideType = 0
  Suppressed = false
  Type = 0
  Type2 = 0
FEATURE [PartDesign::Pad] Pad037
  BaseFeature = -> Pad003
  Direction = (0.866025,-0.5,1e-16)
  Length = 50
  Length2 = 10
  Profile = -> Sketch058
  ReferenceAxis = -> Sketch058 [N_Axis]
  Refine = true
  SideType = 2
  Suppressed = false
  Type = 0
  Type2 = 0
FEATURE [PartDesign::Pad] Pad038
  BaseFeature = -> Pad037
  Direction = (0.866025,0.5,-1e-16)
  Length = 50
  Length2 = 10
  Profile = -> Sketch057
  ReferenceAxis = -> Sketch057 [N_Axis]
  Refine = true
  SideType = 2
  Suppressed = false
  Type = 0
  Type2 = 0
FEATURE [PartDesign::Pocket] Pocket017
  BaseFeature = -> Pad038
  Direction = (0,0,-1)
  Length = 5
  Length2 = 5
  Profile = -> Sketch056
  ReferenceAxis = -> Sketch056 [N_Axis]
  Refine = true
  SideType = 0
  Suppressed = false
  Type = 1
  Type2 = 0
FEATURE [Sketcher::SketchObject] Sketch060
  ArcFitTolerance = 1e-06
  AttachmentSupport = -> [Pad003]
  ExternalTypes = [0]
  FullyConstrained = true
  MakeInternals = false
  MapMode = 5
  Placement = pos=(0,0,-158) rot=(0,0,1;0rad)
  _ExternalGeoVersion = 0
  sketch-geometry (5):
    g0: LineSegment StartX=-120.651 StartY=158.973 StartZ=0 EndX=-77.3494 EndY=183.973 EndZ=0
    g1: LineSegment StartX=-77.3494 StartY=183.973 StartZ=0 EndX=-57.3494 EndY=149.332 EndZ=0
    g2: LineSegment StartX=-57.3494 StartY=149.332 StartZ=0 EndX=-100.651 EndY=124.332 EndZ=0
    g3: LineSegment StartX=-100.651 StartY=124.332 StartZ=0 EndX=-120.651 EndY=158.973 EndZ=0
    g4: LineSegment [constr] StartX=0 StartY=0 StartZ=0 EndX=-115 EndY=199.186 EndZ=0
  constraints (13):
    c: Coincident(g0,g1)
    c: Coincident(g1,g2)
    c: Coincident(g2,g3)
    c: Coincident(g3,g0)
    c: Coincident(g4,g-1)
    c: Angle(g-1,g4) = 2.0944
    c: Symmetric(g0,g0,g4)
    c: Distance(g0) = 50
    c: Parallel(g1,g3)
    c: Distance(g3) = 40
    c: Distance(g4,g2) = 158
    c: Symmetric(g1,g2,g4)
    c: Distance(g4) = 230
FEATURE [PartDesign::CoordinateSystem] Pedestral_Top
  AttacherType = Attacher::AttachEngine3D
  AttachmentOffset = pos=(0,0,0) rot=(0,0,1;-0.523599rad)
  AttachmentSupport = -> [Pocket017]
  MapMode = 45
  Placement = pos=(1.208e-13,1.4e-15,30) rot=(0,0,1;5.75959rad)
FEATURE [PartDesign::Body] Body016  label="Body_Pedestral"
  AllowCompound = false
  Group = -> [Sketch054,Pad034,Sketch055,Pad035,Sketch056,Sketch059,Pad036,Sketch004,Pad003,Sketch060,Sketch058,Pad037,Sketch057,Pad038,Pocket017,Pedestral_Top]
  Origin = -> Origin112
  Tip = -> Pocket017
COMPONENT P10 — recipe-attached ("Body_Pedestral_Connector", modeled in this document).
Construction recipe (the document's own serialized feature program — sketch geometry with constraints, then the solid features built on it; lengths are millimeters unless a unit is written):

FEATURE [Sketcher::SketchObject] Sketch061
  ArcFitTolerance = 1e-06
  AttachmentSupport = -> [YZ_Plane113]
  ExternalTypes = [0]
  FullyConstrained = true
  MakeInternals = false
  MapMode = 5
  Placement = pos=(0,0,0) rot=(0.57735,0.57735,0.57735;2.0944rad)
  _ExternalGeoVersion = 0
  sketch-geometry (1):
    g0: Circle CenterX=0 CenterY=41 CenterZ=0 NormalX=0 NormalY=0 NormalZ=1 AngleXU=0 Radius=2.3
  constraints (3):
    c: PointOnObject(g0,g-2)
    c: Diameter(g0) = 4.6
    c: DistanceY(g-1,g0) = 41
FEATURE [Sketcher::SketchObject] Sketch062
  ArcFitTolerance = 1e-06
  AttachmentSupport = -> [XY_Plane113]
  ExternalTypes = [0]
  FullyConstrained = true
  MakeInternals = false
  MapMode = 5
  _ExternalGeoVersion = 0
  sketch-geometry (2):
    g0: Circle CenterX=0 CenterY=0 CenterZ=0 NormalX=0 NormalY=0 NormalZ=1 AngleXU=0 Radius=25
    g1: Circle CenterX=0 CenterY=0 CenterZ=0 NormalX=0 NormalY=0 NormalZ=1 AngleXU=0 Radius=23
  constraints (4):
    c: Coincident(g0,g-1)
    c: Coincident(g1,g0)
    c: Diameter(g1) = 46
    c: Diameter(g0) = 50
FEATURE [PartDesign::Pad] Pad039
  Direction = (0,0,1)
  Length = 70
  Length2 = 10
  Profile = -> Sketch062
  ReferenceAxis = -> Sketch062 [N_Axis]
  Refine = true
  SideType = 0
  Suppressed = false
  Type = 0
  Type2 = 0
FEATURE [PartDesign::Pocket] Pocket018
  BaseFeature = -> Pad039
  Direction = (-1,0,0)
  Length = 5
  Length2 = 5
  Profile = -> Sketch061
  ReferenceAxis = -> Sketch061 [N_Axis]
  Refine = true
  SideType = 0
  Suppressed = false
  Type = 1
  Type2 = 0
FEATURE [PartDesign::CoordinateSystem] Pedestral_Connector
  AttacherType = Attacher::AttachEngine3D
  AttachmentOffset = pos=(0,0,0) rot=(0,0,-1;1.5708rad)
  AttachmentSupport = -> [Pocket018]
  MapMode = 11
  Placement = pos=(0,0,70) rot=(0,0,1;0rad)
FEATURE [PartDesign::Body] Body017  label="Body_Pedestral_Connector"
  AllowCompound = false
  Group = -> [Sketch061,Sketch062,Pad039,Pocket018,Pedestral_Connector]
  Origin = -> Origin113
  Tip = -> Pocket018
COMPONENT P11 — recipe-attached ("Body_circuit_housing", modeled in this document).
Construction recipe (the document's own serialized feature program — sketch geometry with constraints, then the solid features built on it; lengths are millimeters unless a unit is written):

FEATURE [Sketcher::SketchObject] Sketch069
  ArcFitTolerance = 1e-06
  AttachmentSupport = -> [XY_Plane117]
  ExternalTypes = [0]
  FullyConstrained = true
  MakeInternals = false
  MapMode = 5
  _ExternalGeoVersion = 0
  sketch-geometry (23):
    g0: LineSegment StartX=-48 StartY=31 StartZ=0 EndX=-48 EndY=-31 EndZ=0
    g1: LineSegment StartX=-48 StartY=-31 StartZ=0 EndX=48 EndY=-31 EndZ=0
    g2: LineSegment StartX=48 StartY=-31 StartZ=0 EndX=48 EndY=31 EndZ=0
    g3: LineSegment [constr] StartX=48 StartY=31 StartZ=0 EndX=-48 EndY=31 EndZ=0
    g4: LineSegment StartX=-45 StartY=28 StartZ=0 EndX=-45 EndY=6 EndZ=0
    g5: LineSegment StartX=-45 StartY=6 StartZ=0 EndX=45 EndY=6 EndZ=0
    g6: LineSegment StartX=45 StartY=6 StartZ=0 EndX=45 EndY=28 EndZ=0
    g7: LineSegment StartX=45 StartY=28 StartZ=0 EndX=-45 EndY=28 EndZ=0
    g8: LineSegment StartX=-45 StartY=-6 StartZ=0 EndX=-45 EndY=-28 EndZ=0
    g9: LineSegment StartX=-45 StartY=-28 StartZ=0 EndX=45 EndY=-28 EndZ=0
    g10: LineSegment StartX=45 StartY=-28 StartZ=0 EndX=45 EndY=-6 EndZ=0
    g11: LineSegment StartX=45 StartY=-6 StartZ=0 EndX=-45 EndY=-6 EndZ=0
    g12: Circle CenterX=-36.85 CenterY=0 CenterZ=0 NormalX=0 NormalY=0 NormalZ=1 AngleXU=0 Radius=1.8
    g13: Circle CenterX=36.85 CenterY=0 CenterZ=0 NormalX=0 NormalY=0 NormalZ=1 AngleXU=0 Radius=1.8
    g14: ArcOfCircle CenterX=-27.5 CenterY=38.25 CenterZ=0 NormalX=0 NormalY=0 NormalZ=1 AngleXU=0 Radius=7.25 StartAngle=1.5708 EndAngle=4.71239
    g15: ArcOfCircle CenterX=27.5 CenterY=38.25 CenterZ=0 NormalX=0 NormalY=0 NormalZ=1 AngleXU=0 Radius=7.25 StartAngle=4.71239 EndAngle=7.85398
    g16: LineSegment StartX=-27.5 StartY=45.5 StartZ=0 EndX=27.5 EndY=45.5 EndZ=0
    g17: LineSegment [constr] StartX=-27.5 StartY=31 StartZ=0 EndX=27.5 EndY=31 EndZ=0
    g18: Circle CenterX=-27.5 CenterY=38.25 CenterZ=0 NormalX=0 NormalY=0 NormalZ=1 AngleXU=0 Radius=2.3
    g19: Circle CenterX=27.5 CenterY=38.25 CenterZ=0 NormalX=0 NormalY=0 NormalZ=1 AngleXU=0 Radius=2.3
    g20: Circle CenterX=0 CenterY=38.25 CenterZ=0 NormalX=0 NormalY=0 NormalZ=1 AngleXU=0 Radius=5.3
    g21: LineSegment StartX=-48 StartY=31 StartZ=0 EndX=-27.5 EndY=31 EndZ=0
    g22: LineSegment StartX=48 StartY=31 StartZ=0 EndX=27.5 EndY=31 EndZ=0
  constraints (58):
    c: Coincident(g0,g1)
    c: Coincident(g1,g2)
    c: Coincident(g2,g3)
    c: Coincident(g3,g0)
    c: Vertical(g0)
    c: Vertical(g2)
    c: Horizontal(g1)
    c: Horizontal(g3)
    c: Symmetric(g0,g1,g-1)
    c: DistanceX(g3,g3) = 96
    c: DistanceY(g2,g2) = 62
    c: Coincident(g4,g5)
    c: Coincident(g5,g6)
    c: Coincident(g6,g7)
    c: Coincident(g7,g4)
    c: Vertical(g4)
    c: Vertical(g6)
    c: Horizontal(g5)
    c: Horizontal(g7)
    c: Coincident(g8,g9)
    c: Coincident(g9,g10)
    c: Coincident(g10,g11)
    c: Coincident(g11,g8)
    c: Vertical(g8)
    c: Vertical(g10)
    c: Horizontal(g9)
    c: Horizontal(g11)
    c: Symmetric(g8,g4,g-1)
    c: Equal(g4,g8)
    c: Equal(g5,g11)
    c: DistanceX(g0,g4) = 3
    c: DistanceX(g6,g2) = 3
    c: DistanceY(g1,g9) = 3
    c: DistanceY(g10,g5) = 12
    c: PointOnObject(g12,g-1)
    c: Symmetric(g12,g13,g-2)
    c: Equal(g12,g13)
    c: DistanceX(g12,g13) = 73.7
    c: Diameter(g12) = 3.6
    c: Tangent(g14,g16) = 1.5708
    c: Tangent(g14,g17) = -1.5708
    c: Tangent(g15,g16) = 1.5708
    c: Tangent(g15,g17) = -1.5708
    c: Equal(g14,g15)
    c: Symmetric(g14,g15,g-2)
    c: Coincident(g18,g14)
    c: Coincident(g19,g15)
    c: PointOnObject(g20,g-2)
    c: Equal(g18,g19)
    c: Diameter(g20) = 10.6
    c: DistanceX(g16,g16) = 55
    c: DistanceY(g20,g15) = 0
    c: Diameter(g14) = 14.5
    c: Diameter(g18) = 4.6
    c: Coincident(g21,g0)
    c: Coincident(g21,g14)
    c: Coincident(g22,g2)
    c: Tangent(g22,g15) = 1.5708
FEATURE [PartDesign::Pad] Pad043
  Direction = (0,0,1)
  Length = 10
  Length2 = 10
  Profile = -> Sketch069
  ReferenceAxis = -> Sketch069 [N_Axis]
  Refine = true
  SideType = 0
  Suppressed = false
  Type = 0
  Type2 = 0
FEATURE [Sketcher::SketchObject] Sketch070
  ArcFitTolerance = 1e-06
  AttachmentSupport = -> [Pad043]
  ExternalGeometry = -> [Pad043]
  ExternalTypes = [0]
  FullyConstrained = true
  MakeInternals = false
  MapMode = 5
  Placement = pos=(0,0,10) rot=(0,0,1;0rad)
  _ExternalGeoVersion = 0
  sketch-geometry (4):
    g0: LineSegment StartX=-45 StartY=6 StartZ=0 EndX=-45 EndY=-6 EndZ=0
    g1: LineSegment StartX=-45 StartY=-6 StartZ=0 EndX=45 EndY=-6 EndZ=0
    g2: LineSegment StartX=45 StartY=-6 StartZ=0 EndX=45 EndY=6 EndZ=0
    g3: LineSegment StartX=45 StartY=6 StartZ=0 EndX=-45 EndY=6 EndZ=0
  constraints (10):
    c: Coincident(g0,g1)
    c: Coincident(g1,g2)
    c: Coincident(g2,g3)
    c: Coincident(g3,g0)
    c: Vertical(g0)
    c: Vertical(g2)
    c: Horizontal(g1)
    c: Horizontal(g3)
    c: Coincident(g1,g-4)
    c: Coincident(g0,g-3)
FEATURE [PartDesign::Pocket] Pocket021
  BaseFeature = -> Pad043
  Direction = (0,0,-1)
  Length = 7
  Length2 = 5
  Profile = -> Sketch070
  ReferenceAxis = -> Sketch070 [N_Axis]
  Refine = true
  SideType = 0
  Suppressed = false
  Type = 0
  Type2 = 0
FEATURE [Sketcher::SketchObject] Sketch071
  ArcFitTolerance = 1e-06
  AttachmentSupport = -> [Pocket021]
  ExternalGeometry = -> [Pocket021]
  ExternalTypes = [0]
  FullyConstrained = true
  MakeInternals = false
  MapMode = 5
  Placement = pos=(0,0,10) rot=(0,0,1;0rad)
  _ExternalGeoVersion = 0
  sketch-geometry (4):
    g0: LineSegment StartX=-35 StartY=45.5 StartZ=0 EndX=-35 EndY=31 EndZ=0
    g1: LineSegment StartX=-35 StartY=31 StartZ=0 EndX=35 EndY=31 EndZ=0
    g2: LineSegment StartX=35 StartY=31 StartZ=0 EndX=35 EndY=45.5 EndZ=0
    g3: LineSegment StartX=35 StartY=45.5 StartZ=0 EndX=-35 EndY=45.5 EndZ=0
  constraints (12):
    c: Coincident(g0,g1)
    c: Coincident(g1,g2)
    c: Coincident(g2,g3)
    c: Coincident(g3,g0)
    c: Vertical(g0)
    c: Vertical(g2)
    c: Horizontal(g1)
    c: Horizontal(g3)
    c: PointOnObject(g-4,g3)
    c: PointOnObject(g-3,g1)
    c: DistanceX(g0,g-1) = 35
    c: DistanceX(g-1,g2) = 35
FEATURE [PartDesign::Pocket] Pocket022
  BaseFeature = -> Pocket021
  Direction = (0,0,-1)
  Length = 5
  Length2 = 5
  Profile = -> Sketch071
  ReferenceAxis = -> Sketch071 [N_Axis]
  Refine = true
  SideType = 0
  Suppressed = false
  Type = 0
  Type2 = 0
FEATURE [PartDesign::CoordinateSystem] LCS_Circuit_Housing
  AttacherType = Attacher::AttachEngine3D
  AttachmentSupport = -> [Pocket022]
  MapMode = 45
  Placement = pos=(-27.5,38.25,5) rot=(0,0,1;0rad)
FEATURE [PartDesign::CoordinateSystem] LCS_Circuit_Button
  AttacherType = Attacher::AttachEngine3D
  AttachmentSupport = -> [Pocket022]
  MapMode = 45
  Placement = pos=(-4e-16,38.25,4.5869) rot=(0,0,1;1.5708rad)
FEATURE [PartDesign::Body] Body019  label="Body_circuit_housing"
  AllowCompound = false
  Group = -> [Sketch069,Pad043,Sketch070,Pocket021,Sketch071,Pocket022,LCS_Circuit_Housing,LCS_Circuit_Button]
  Origin = -> Origin231
  Tip = -> Pocket022
COMPONENT P12 — recipe-attached ("Body_Button_Round", modeled in this document).
Construction recipe (the document's own serialized feature program — sketch geometry with constraints, then the solid features built on it; lengths are millimeters unless a unit is written):

FEATURE [Sketcher::SketchObject] Sketch072
  ArcFitTolerance = 1e-06
  AttachmentSupport = -> [Origin235]
  ExternalTypes = [0]
  FullyConstrained = true
  MakeInternals = false
  MapMode = 5
  _ExternalGeoVersion = 1
  sketch-geometry (1):
    g0: Circle CenterX=0 CenterY=0 CenterZ=0 NormalX=0 NormalY=0 NormalZ=1 AngleXU=0 Radius=7.5
  constraints (2):
    c: Coincident(g0,g-1)
    c: Diameter(g0) = 15
FEATURE [PartDesign::Pad] Pad044
  Direction = (0,0,1)
  Length = 8
  Length2 = 10
  Profile = -> Sketch072
  ReferenceAxis = -> Sketch072 [N_Axis]
  Refine = true
  SideType = 0
  Suppressed = false
  Type = 0
  Type2 = 0
FEATURE [Sketcher::SketchObject] Sketch073
  ArcFitTolerance = 1e-06
  AttachmentSupport = -> [Pad044]
  ExternalTypes = [0]
  FullyConstrained = true
  MakeInternals = false
  MapMode = 5
  Placement = pos=(0,0,8) rot=(0,0,1;0rad)
  _ExternalGeoVersion = 1
  sketch-geometry (1):
    g0: Circle CenterX=0 CenterY=0 CenterZ=0 NormalX=0 NormalY=0 NormalZ=1 AngleXU=0 Radius=5
  constraints (2):
    c: Coincident(g0,g-1)
    c: Diameter(g0) = 10
FEATURE [PartDesign::Pad] Pad045
  BaseFeature = -> Pad044
  Direction = (0,0,1)
  Length = 5
  Length2 = 10
  Profile = -> Sketch073
  ReferenceAxis = -> Sketch073 [N_Axis]
  Refine = true
  SideType = 0
  Suppressed = false
  Type = 0
  Type2 = 0
FEATURE [Sketcher::SketchObject] Sketch074
  ArcFitTolerance = 1e-06
  AttachmentSupport = -> [Pad045]
  ExternalTypes = [0]
  FullyConstrained = true
  MakeInternals = false
  MapMode = 5
  Placement = pos=(0,0,0) rot=(1,0,0;3.14159rad)
  _ExternalGeoVersion = 1
  sketch-geometry (1):
    g0: Circle CenterX=0 CenterY=0 CenterZ=0 NormalX=0 NormalY=0 NormalZ=1 AngleXU=0 Radius=4.3
  constraints (2):
    c: Coincident(g0,g-1)
    c: Diameter(g0) = 8.6
FEATURE [PartDesign::Pad] Pad046
  BaseFeature = -> Pad045
  Direction = (0,0,-1)
  Length = 13
  Length2 = 10
  Profile = -> Sketch074
  ReferenceAxis = -> Sketch074 [N_Axis]
  Refine = true
  SideType = 0
  Suppressed = false
  Type = 0
  Type2 = 0
FEATURE [Sketcher::SketchObject] Sketch075
  ArcFitTolerance = 1e-06
  AttachmentSupport = -> [Pad046]
  ExternalTypes = [0]
  FullyConstrained = true
  MakeInternals = false
  MapMode = 5
  Placement = pos=(0,0,-13) rot=(1,0,0;3.14159rad)
  _ExternalGeoVersion = 1
  sketch-geometry (8):
    g0: LineSegment StartX=-2.2 StartY=2 StartZ=0 EndX=-2.2 EndY=-2 EndZ=0
    g1: LineSegment StartX=-2.2 StartY=-2 StartZ=0 EndX=-2 EndY=-2 EndZ=0
    g2: LineSegment StartX=-2 StartY=-2 StartZ=0 EndX=-2 EndY=2 EndZ=0
    g3: LineSegment StartX=-2 StartY=2 StartZ=0 EndX=-2.2 EndY=2 EndZ=0
    g4: LineSegment StartX=2 StartY=2 StartZ=0 EndX=2 EndY=-2 EndZ=0
    g5: LineSegment StartX=2 StartY=-2 StartZ=0 EndX=2.2 EndY=-2 EndZ=0
    g6: LineSegment StartX=2.2 StartY=-2 StartZ=0 EndX=2.2 EndY=2 EndZ=0
    g7: LineSegment StartX=2.2 StartY=2 StartZ=0 EndX=2 EndY=2 EndZ=0
  constraints (22):
    c: Coincident(g0,g1)
    c: Coincident(g1,g2)
    c: Coincident(g2,g3)
    c: Coincident(g3,g0)
    c: Vertical(g0)
    c: Vertical(g2)
    c: Horizontal(g1)
    c: Horizontal(g3)
    c: Coincident(g4,g5)
    c: Coincident(g5,g6)
    c: Coincident(g6,g7)
    c: Coincident(g7,g4)
    c: Vertical(g4)
    c: Horizontal(g5)
    c: Horizontal(g7)
    c: Symmetric(g6,g5,g-1)
    c: Symmetric(g2,g4,g-2)
    c: Equal(g2,g4)
    c: Equal(g3,g7)
    c: DistanceX(g3,g3) = 0.2
    c: DistanceY(g0,g0) = 4
    c: DistanceX(g1,g4) = 4
FEATURE [PartDesign::Pad] Pad047
  BaseFeature = -> Pad046
  Direction = (0,0,-1)
  Length = 8
  Length2 = 10
  Profile = -> Sketch075
  ReferenceAxis = -> Sketch075 [N_Axis]
  Refine = true
  SideType = 0
  Suppressed = false
  Type = 0
  Type2 = 0
FEATURE [Sketcher::SketchObject] Sketch076
  ArcFitTolerance = 1e-06
  AttachmentSupport = -> [Pad047]
  ExternalTypes = [0]
  FullyConstrained = true
  MakeInternals = false
  MapMode = 5
  Placement = pos=(2.2,0,0) rot=(0.57735,0.57735,0.57735;2.0944rad)
  _ExternalGeoVersion = 1
  sketch-geometry (1):
    g0: Circle CenterX=0 CenterY=-18 CenterZ=0 NormalX=0 NormalY=0 NormalZ=1 AngleXU=0 Radius=1
  constraints (3):
    c: PointOnObject(g0,g-2)
    c: Diameter(g0) = 2
    c: DistanceY(g0,g-1) = 18
FEATURE [PartDesign::Pocket] Pocket023
  BaseFeature = -> Pad047
  Direction = (-1,0,0)
  Length = 5
  Length2 = 5
  Profile = -> Sketch076
  ReferenceAxis = -> Sketch076 [N_Axis]
  Refine = true
  SideType = 0
  Suppressed = false
  Type = 1
  Type2 = 0
FEATURE [PartDesign::Fillet] Fillet011
  Base = -> Pocket023 [Edge35,Edge25,Edge30,Edge20]
  BaseFeature = -> Pocket023
  Radius = 6.5
  Refine = true
  SupportTransform = false
  Suppressed = false
  UseAllEdges = false
FEATURE [PartDesign::CoordinateSystem] LCS_Button
  AttacherType = Attacher::AttachEngine3D
  AttachmentSupport = -> [Fillet011]
  MapMode = 45
  Placement = pos=(3.05e-14,-1e-16,10) rot=(0,0,1;0rad)
FEATURE [PartDesign::Body] Body020  label="Body_Button_Round"
  AllowCompound = false
  Group = -> [Sketch072,Pad044,Sketch073,Pad045,Sketch074,Pad046,Sketch075,Pad047,Sketch076,Pocket023,Fillet011,LCS_Button]
  Origin = -> Origin235
  Tip = -> Fillet011
COMPONENT P13 — recipe-attached ("Body_Cylinders", modeled in this document).
Construction recipe (the document's own serialized feature program — sketch geometry with constraints, then the solid features built on it; lengths are millimeters unless a unit is written):

FEATURE [PartDesign::CoordinateSystem] LCS_Origin001
  AttacherType = Attacher::AttachEngine3D
  AttachmentSupport = -> [X_Axis116]
  MapMode = 2
FEATURE [Sketcher::SketchObject] Sketch068
  ArcFitTolerance = 1e-06
  AttachmentSupport = -> [Origin228]
  ExternalTypes = [0]
  FullyConstrained = true
  MakeInternals = false
  MapMode = 5
  _ExternalGeoVersion = 1
  sketch-geometry (1):
    g0: Circle CenterX=0 CenterY=0 CenterZ=0 NormalX=0 NormalY=0 NormalZ=1 AngleXU=0 Radius=4.2
  constraints (2):
    c: Coincident(g0,g-1)
    c: Diameter(g0) = 8.4
FEATURE [PartDesign::Pad] Pad042
  Direction = (0,0,1)
  Length = 30
  Length2 = 10
  Profile = -> Sketch068
  ReferenceAxis = -> Sketch068 [N_Axis]
  Refine = true
  SideType = 0
  Suppressed = false
  Type = 0
  Type2 = 0
FEATURE [PartDesign::Hole] Hole
  BaseFeature = -> Pad042
  BaseProfileType = 7
  CustomThreadClearance = 0
  Depth = 30
  DepthType = 0
  Diameter = 4
  DrillForDepth = false
  DrillPoint = 0
  DrillPointAngle = 118
  HoleCutCountersinkAngle = 90
  HoleCutCustomValues = false
  HoleCutDepth = 0
  HoleCutDiameter = 0
  HoleCutType = 0
  ModelThread = false
  Profile = -> Pad042 [Face3]
  Refine = true
  Suppressed = false
  Tapered = false
  TaperedAngle = 90
  ThreadClass = 0
  ThreadDepth = 30
  ThreadDepthType = 0
  ThreadDiameter = 4
  ThreadDirection = 0
  ThreadFit = 0
  ThreadSize = 0
  ThreadType = 0
  Threaded = false
  UseCustomThreadClearance = false
FEATURE [PartDesign::Body] Body_Cylinders
  AllowCompound = true
  Group = -> [LCS_Origin001,Sketch068,Pad042,Hole]
  Origin = -> Origin228
  Tip = -> Hole
COMPONENT P14 — geometry summary ("PCB"; no construction recipe available for this part):
  bounding box: 44.3 x 17.8 x 4.8 mm
  tessellated surface: 31,666 triangles
  volume: 1543 mm^3 (41% of its bounding box)
COMPONENT P15 — geometry summary ("kiCad_Board"; no construction recipe available for this part):
  bounding box: 88.0 x 51.5 x 17.3 mm
  tessellated surface: 2,790 triangles
  volume: 8126 mm^3 (10% of its bounding box)
COMPONENT P16 — geometry summary ("main_Circuit-kicad"; no construction recipe available for this part):
  bounding box: 64.8 x 42.8 x 24.0 mm
  tessellated surface: 4,266 triangles
  volume: 13109602566308300294308585964398251072344487416303549499351432675718616053546067294405155264799965184 mm^3 (19679265341829405668994878035270094576215740122560207115929017522149239054776622481610748897263616% of its bounding box)
PROVENANCE & LICENSES
A FreeCAD (.FCStd) document from a public repository crawl; recipes are the document's own serialized feature recipes (and, for linked parts, companion documents' recipes).
License: gpl-3.0.
